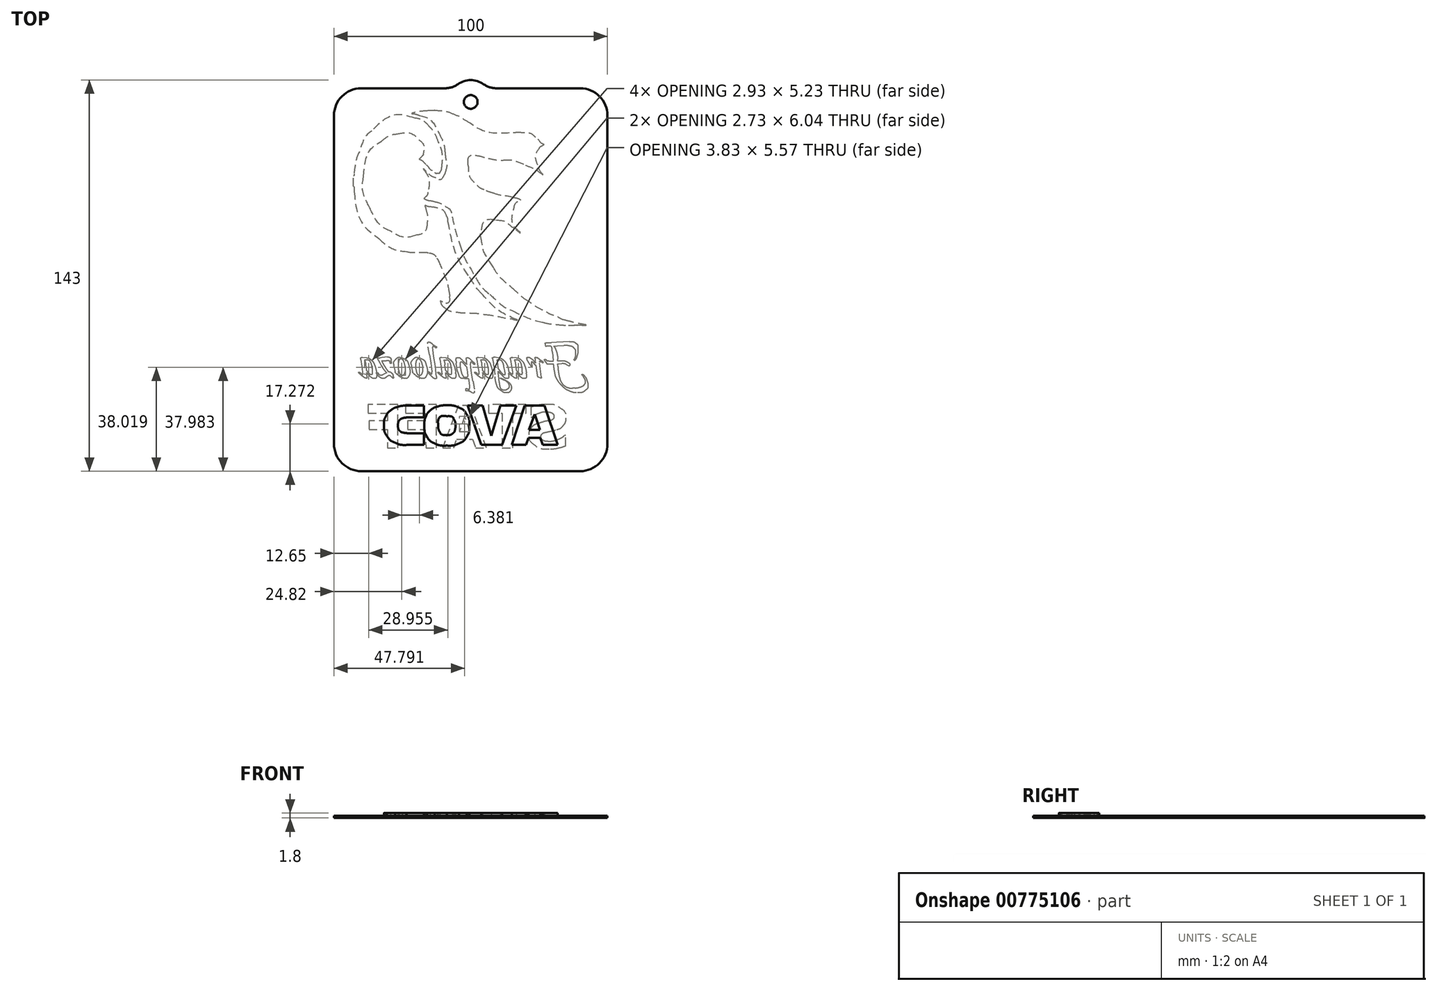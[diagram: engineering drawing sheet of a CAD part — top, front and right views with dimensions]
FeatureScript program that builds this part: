
annotation { "Feature Type Name" : "Feature", "Feature Type Description" : "" }
export const myFeature = defineFeature(function(context is Context, id is Id, definition is map)
    precondition{}
    {
        {
            var Q0;
            Q0=qCreatedBy(makeId("Top.planeOp"),FACE);
            var sketch = newSketch(context, id + "F0", { "sketchPlane" : qUnion([Q0])});
            skLineSegment(sketch, "E0.bottom", {"start": v(-40, 70) * mm, "end": v(-9.33, 70) * mm});
            skLineSegment(sketch, "E0.top", {"start": v(-40, -70) * mm, "end": v(40, -70) * mm});
            skLineSegment(sketch, "E0.left", {"start": v(-50, 60) * mm, "end": v(-50, -60) * mm});
            skLineSegment(sketch, "E0.right", {"start": v(50, 60) * mm, "end": v(50, -60) * mm});
            skPoint(sketch, "E0.middle", {"position": v(0, 0) * mm});
            skCircle(sketch, "E1", {"center": v(0, 65) * mm, "radius": 2.5 * mm});
            skPoint(sketch, "E2.visualSharp", {"position": v(-50, 70) * mm});
            skArc(sketch, "E2.filletArc", {"start": v(-40, 70) * mm, "mid": v(-47.07, 67.07) * mm, "end": v(-50, 60) * mm});
            skPoint(sketch, "E3.visualSharp", {"position": v(50, 70) * mm});
            skArc(sketch, "E3.filletArc", {"start": v(50, 60) * mm, "mid": v(47.07, 67.07) * mm, "end": v(40, 70) * mm});
            skPoint(sketch, "E4.visualSharp", {"position": v(50, -70) * mm});
            skArc(sketch, "E4.filletArc", {"start": v(40, -70) * mm, "mid": v(47.07, -67.07) * mm, "end": v(50, -60) * mm});
            skPoint(sketch, "E5.visualSharp", {"position": v(-50, -70) * mm});
            skArc(sketch, "E5.filletArc", {"start": v(-50, -60) * mm, "mid": v(-47.07, -67.07) * mm, "end": v(-40, -70) * mm});
            skArc(sketch, "E6", {"start": v(-4.66, 71.5) * mm, "mid": v(0, 73) * mm, "end": v(4.66, 71.5) * mm});
            skArc(sketch, "E7.filletArc", {"start": v(-9.33, 70) * mm, "mid": v(-6.88, 70.38) * mm, "end": v(-4.66, 71.5) * mm});
            skLineSegment(sketch, "E8", {"start": v(40, 70) * mm, "end": v(9.33, 70) * mm});
            skArc(sketch, "E9.filletArc", {"start": v(4.66, 71.5) * mm, "mid": v(6.88, 70.38) * mm, "end": v(9.33, 70) * mm});
            skSolve(sketch);
        }
        {
            var Q0;
            Q0=qCreatedBy(makeId("Top.planeOp"),FACE);
            var sketch = newSketch(context, id + "F1", { "sketchPlane" : qUnion([Q0])});
            skLineSegment(sketch, "E10", {"start": v(38.17, -16.7) * mm, "end": v(38.78, -16.7) * mm});
            skLineSegment(sketch, "E11", {"start": v(-13.07, 61.96) * mm, "end": v(-13.17, 61.96) * mm});
            skLineSegment(sketch, "E12", {"start": v(-14.17, 61.96) * mm, "end": v(-14.37, 61.96) * mm});
            skLineSegment(sketch, "E13", {"start": v(-42.85, 37.93) * mm, "end": v(-42.85, 36.81) * mm});
            skLineSegment(sketch, "E14", {"start": v(-42.85, 35.49) * mm, "end": v(-42.85, 34.98) * mm});
            skLineSegment(sketch, "E15", {"start": v(-42.85, 34.78) * mm, "end": v(-42.85, 34.16) * mm});
            skLineSegment(sketch, "E16", {"start": v(40.64, -16.7) * mm, "end": v(40.63, -16.62) * mm});
            skLineSegment(sketch, "E17", {"start": v(38.83, -16.7) * mm, "end": v(40.64, -16.7) * mm});
            skLineSegment(sketch, "E18", {"start": v(-42.85, 36.81) * mm, "end": v(-42.85, 35.49) * mm});
            skLineSegment(sketch, "E19", {"start": v(-13.21, 61.96) * mm, "end": v(-14.22, 61.96) * mm});
            skLineSegment(sketch, "E20", {"start": v(-42.85, 34.98) * mm, "end": v(-42.85, 34.77) * mm});
            skLineSegment(sketch, "E21", {"start": v(36.03, -31.52) * mm, "end": v(35.01, -30.98) * mm});
            skLineSegment(sketch, "E22", {"start": v(33.37, -30.7) * mm, "end": v(32.17, -30.75) * mm});
            skLineSegment(sketch, "E23", {"start": v(32.17, -30.75) * mm, "end": v(30.92, -30.82) * mm});
            skLineSegment(sketch, "E24", {"start": v(30.92, -30.82) * mm, "end": v(27.9, -30.82) * mm});
            skLineSegment(sketch, "E25", {"start": v(27.9, -30.82) * mm, "end": v(27.52, -30.26) * mm});
            skLineSegment(sketch, "E26", {"start": v(26.88, -29.35) * mm, "end": v(26.9, -29.28) * mm});
            skLineSegment(sketch, "E27", {"start": v(30.32, -29.76) * mm, "end": v(31.57, -29.76) * mm});
            skLineSegment(sketch, "E28", {"start": v(31.57, -29.76) * mm, "end": v(33.15, -29.76) * mm});
            skLineSegment(sketch, "E29", {"start": v(33.15, -29.76) * mm, "end": v(34.41, -29.76) * mm});
            skLineSegment(sketch, "E30", {"start": v(34.05, -24.06) * mm, "end": v(31.6, -24.16) * mm});
            skLineSegment(sketch, "E31", {"start": v(31.6, -24.16) * mm, "end": v(29.36, -24.3) * mm});
            skLineSegment(sketch, "E32", {"start": v(27.3, -24.39) * mm, "end": v(27.09, -23.13) * mm});
            skLineSegment(sketch, "E33", {"start": v(29.45, -22.97) * mm, "end": v(31.35, -22.93) * mm});
            skLineSegment(sketch, "E34", {"start": v(31.35, -22.93) * mm, "end": v(33.78, -22.78) * mm});
            skLineSegment(sketch, "E35", {"start": v(33.78, -22.78) * mm, "end": v(36.14, -22.66) * mm});
            skLineSegment(sketch, "E36", {"start": v(38.04, -29.5) * mm, "end": v(37.7, -29.32) * mm});
            skLineSegment(sketch, "E37", {"start": v(30.25, -30.2) * mm, "end": v(29.88, -26.54) * mm});
            skLineSegment(sketch, "E38", {"start": v(29.55, -24.56) * mm, "end": v(29.3, -24.3) * mm});
            skLineSegment(sketch, "E39", {"start": v(29.18, -23.96) * mm, "end": v(29.55, -24.04) * mm});
            skLineSegment(sketch, "E40", {"start": v(31.76, -29.06) * mm, "end": v(31.88, -31.82) * mm});
            skLineSegment(sketch, "E41", {"start": v(37.27, -39.71) * mm, "end": v(38.3, -39.63) * mm});
            skLineSegment(sketch, "E42", {"start": v(41.15, -35.4) * mm, "end": v(40.78, -34.92) * mm});
            skLineSegment(sketch, "E43", {"start": v(40.78, -34.92) * mm, "end": v(40.72, -34.76) * mm});
            skLineSegment(sketch, "E44", {"start": v(23.56, -29.53) * mm, "end": v(23.5, -28.89) * mm});
            skLineSegment(sketch, "E45", {"start": v(24.23, -28.54) * mm, "end": v(25.22, -29.23) * mm});
            skLineSegment(sketch, "E46", {"start": v(25.22, -29.23) * mm, "end": v(26.33, -30.01) * mm});
            skLineSegment(sketch, "E47", {"start": v(26.48, -30.3) * mm, "end": v(26.4, -30.34) * mm});
            skLineSegment(sketch, "E48", {"start": v(26.4, -30.34) * mm, "end": v(26.3, -30.32) * mm});
            skLineSegment(sketch, "E49", {"start": v(26.3, -30.32) * mm, "end": v(26.17, -30.3) * mm});
            skLineSegment(sketch, "E50", {"start": v(25.15, -30.3) * mm, "end": v(25.53, -33.54) * mm});
            skLineSegment(sketch, "E51", {"start": v(25.53, -33.54) * mm, "end": v(25.79, -35.64) * mm});
            skLineSegment(sketch, "E52", {"start": v(25.88, -36) * mm, "end": v(24.4, -35.44) * mm});
            skLineSegment(sketch, "E53", {"start": v(23.19, -29.85) * mm, "end": v(23.89, -30.75) * mm});
            skLineSegment(sketch, "E54", {"start": v(23.65, -31.18) * mm, "end": v(23.19, -30.77) * mm});
            skLineSegment(sketch, "E55", {"start": v(15.9, -29.4) * mm, "end": v(15.4, -29.4) * mm});
            skLineSegment(sketch, "E56", {"start": v(15.4, -29.4) * mm, "end": v(15.02, -29.33) * mm});
            skLineSegment(sketch, "E57", {"start": v(15.24, -28.42) * mm, "end": v(16.71, -28.55) * mm});
            skLineSegment(sketch, "E58", {"start": v(17.3, -34.56) * mm, "end": v(16.63, -33.84) * mm});
            skLineSegment(sketch, "E59", {"start": v(16.01, -32.3) * mm, "end": v(16.46, -32.84) * mm});
            skLineSegment(sketch, "E60", {"start": v(16.96, -29.4) * mm, "end": v(16.5, -29.4) * mm});
            skLineSegment(sketch, "E61", {"start": v(16.5, -29.4) * mm, "end": v(15.9, -29.4) * mm});
            skLineSegment(sketch, "E62", {"start": v(16.38, -31.1) * mm, "end": v(16.6, -32.79) * mm});
            skLineSegment(sketch, "E63", {"start": v(16.6, -32.79) * mm, "end": v(16.8, -34.4) * mm});
            skLineSegment(sketch, "E64", {"start": v(16.8, -34.4) * mm, "end": v(16.85, -35.3) * mm});
            skLineSegment(sketch, "E65", {"start": v(14.85, -34.45) * mm, "end": v(15.26, -34.75) * mm});
            skLineSegment(sketch, "E66", {"start": v(15.33, -34.51) * mm, "end": v(15.26, -33.72) * mm});
            skLineSegment(sketch, "E67", {"start": v(15.26, -33.72) * mm, "end": v(14.93, -31.64) * mm});
            skLineSegment(sketch, "E68", {"start": v(14.93, -31.64) * mm, "end": v(14.54, -29.14) * mm});
            skLineSegment(sketch, "E69", {"start": v(9.13, -29.4) * mm, "end": v(8.63, -29.4) * mm});
            skLineSegment(sketch, "E70", {"start": v(8.63, -29.4) * mm, "end": v(8.27, -29.31) * mm});
            skLineSegment(sketch, "E71", {"start": v(8.04, -29.08) * mm, "end": v(7.89, -28.74) * mm});
            skLineSegment(sketch, "E72", {"start": v(8.47, -28.35) * mm, "end": v(8.95, -28.35) * mm});
            skLineSegment(sketch, "E73", {"start": v(8.95, -28.35) * mm, "end": v(9.46, -28.52) * mm});
            skLineSegment(sketch, "E74", {"start": v(9.46, -28.52) * mm, "end": v(10.14, -28.6) * mm});
            skLineSegment(sketch, "E75", {"start": v(11.28, -34.74) * mm, "end": v(10.47, -33.88) * mm});
            skLineSegment(sketch, "E76", {"start": v(9.69, -32.05) * mm, "end": v(10.37, -32.95) * mm});
            skLineSegment(sketch, "E77", {"start": v(10.37, -32.95) * mm, "end": v(11.14, -33.94) * mm});
            skLineSegment(sketch, "E78", {"start": v(12.6, -34.13) * mm, "end": v(12.52, -33.32) * mm});
            skLineSegment(sketch, "E79", {"start": v(12.52, -33.32) * mm, "end": v(12.29, -32.26) * mm});
            skLineSegment(sketch, "E80", {"start": v(12.29, -32.26) * mm, "end": v(12.13, -31.6) * mm});
            skLineSegment(sketch, "E81", {"start": v(10.33, -29.4) * mm, "end": v(9.77, -29.4) * mm});
            skLineSegment(sketch, "E82", {"start": v(9.77, -29.4) * mm, "end": v(9.13, -29.4) * mm});
            skLineSegment(sketch, "E83", {"start": v(9.46, -28.84) * mm, "end": v(9.77, -30.97) * mm});
            skLineSegment(sketch, "E84", {"start": v(9.77, -30.97) * mm, "end": v(10.1, -34.04) * mm});
            skLineSegment(sketch, "E85", {"start": v(10.1, -34.04) * mm, "end": v(10.34, -36.29) * mm});
            skLineSegment(sketch, "E86", {"start": v(10.34, -36.29) * mm, "end": v(10.47, -37.68) * mm});
            skLineSegment(sketch, "E87", {"start": v(12.25, -36.7) * mm, "end": v(11.22, -36.28) * mm});
            skLineSegment(sketch, "E88", {"start": v(10.66, -36) * mm, "end": v(10.7, -35.94) * mm});
            skLineSegment(sketch, "E89", {"start": v(8.88, -35.3) * mm, "end": v(8.5, -31.75) * mm});
            skLineSegment(sketch, "E90", {"start": v(3.54, -29.4) * mm, "end": v(3.04, -29.4) * mm});
            skLineSegment(sketch, "E91", {"start": v(3.04, -29.4) * mm, "end": v(2.67, -29.33) * mm});
            skLineSegment(sketch, "E92", {"start": v(2.88, -28.42) * mm, "end": v(4.36, -28.55) * mm});
            skLineSegment(sketch, "E93", {"start": v(4.94, -34.56) * mm, "end": v(4.28, -33.84) * mm});
            skLineSegment(sketch, "E94", {"start": v(3.66, -32.3) * mm, "end": v(4.1, -32.84) * mm});
            skLineSegment(sketch, "E95", {"start": v(4.6, -29.4) * mm, "end": v(4.14, -29.4) * mm});
            skLineSegment(sketch, "E96", {"start": v(4.14, -29.4) * mm, "end": v(3.54, -29.4) * mm});
            skLineSegment(sketch, "E97", {"start": v(4.02, -31.1) * mm, "end": v(4.25, -32.79) * mm});
            skLineSegment(sketch, "E98", {"start": v(4.25, -32.79) * mm, "end": v(4.44, -34.4) * mm});
            skLineSegment(sketch, "E99", {"start": v(4.44, -34.4) * mm, "end": v(4.5, -35.3) * mm});
            skLineSegment(sketch, "E100", {"start": v(2.5, -34.45) * mm, "end": v(2.9, -34.75) * mm});
            skLineSegment(sketch, "E101", {"start": v(2.98, -34.51) * mm, "end": v(2.9, -33.72) * mm});
            skLineSegment(sketch, "E102", {"start": v(2.9, -33.72) * mm, "end": v(2.58, -31.64) * mm});
            skLineSegment(sketch, "E103", {"start": v(2.58, -31.64) * mm, "end": v(2.19, -29.14) * mm});
            skLineSegment(sketch, "E104", {"start": v(-0.07, -30.77) * mm, "end": v(0.03, -32.01) * mm});
            skLineSegment(sketch, "E105", {"start": v(0.03, -32.01) * mm, "end": v(0.35, -34.14) * mm});
            skLineSegment(sketch, "E106", {"start": v(0.35, -34.14) * mm, "end": v(0.85, -37.11) * mm});
            skLineSegment(sketch, "E107", {"start": v(0.96, -41.4) * mm, "end": v(0.32, -41.16) * mm});
            skLineSegment(sketch, "E108", {"start": v(-0.43, -39.67) * mm, "end": v(-0.47, -38.83) * mm});
            skLineSegment(sketch, "E109", {"start": v(-0.47, -38.83) * mm, "end": v(-0.77, -36.7) * mm});
            skLineSegment(sketch, "E110", {"start": v(-0.77, -36.7) * mm, "end": v(-1.14, -33.74) * mm});
            skLineSegment(sketch, "E111", {"start": v(-1.14, -33.74) * mm, "end": v(-1.34, -32.16) * mm});
            skLineSegment(sketch, "E112", {"start": v(-1.34, -32.16) * mm, "end": v(-1.56, -30.34) * mm});
            skLineSegment(sketch, "E113", {"start": v(-1.56, -30.34) * mm, "end": v(-1.62, -29.37) * mm});
            skLineSegment(sketch, "E114", {"start": v(-0.41, -35.45) * mm, "end": v(-0.36, -35.65) * mm});
            skLineSegment(sketch, "E115", {"start": v(-0.18, -36.1) * mm, "end": v(-0.24, -36.16) * mm});
            skLineSegment(sketch, "E116", {"start": v(-0.24, -36.16) * mm, "end": v(-0.31, -36.19) * mm});
            skLineSegment(sketch, "E117", {"start": v(-0.31, -36.19) * mm, "end": v(-0.7, -36.11) * mm});
            skLineSegment(sketch, "E118", {"start": v(-0.7, -36.11) * mm, "end": v(-1.4, -36.11) * mm});
            skLineSegment(sketch, "E119", {"start": v(-1.4, -36.11) * mm, "end": v(-2.27, -36.11) * mm});
            skLineSegment(sketch, "E120", {"start": v(-2.53, -30.03) * mm, "end": v(-1.85, -30.67) * mm});
            skLineSegment(sketch, "E121", {"start": v(-9.94, -29.4) * mm, "end": v(-10.44, -29.4) * mm});
            skLineSegment(sketch, "E122", {"start": v(-10.44, -29.4) * mm, "end": v(-10.8, -29.33) * mm});
            skLineSegment(sketch, "E123", {"start": v(-10.6, -28.42) * mm, "end": v(-9.12, -28.55) * mm});
            skLineSegment(sketch, "E124", {"start": v(-8.54, -34.56) * mm, "end": v(-9.2, -33.84) * mm});
            skLineSegment(sketch, "E125", {"start": v(-9.82, -32.3) * mm, "end": v(-9.37, -32.84) * mm});
            skLineSegment(sketch, "E126", {"start": v(-8.87, -29.4) * mm, "end": v(-9.34, -29.4) * mm});
            skLineSegment(sketch, "E127", {"start": v(-9.34, -29.4) * mm, "end": v(-9.94, -29.4) * mm});
            skLineSegment(sketch, "E128", {"start": v(-9.46, -31.1) * mm, "end": v(-9.23, -32.79) * mm});
            skLineSegment(sketch, "E129", {"start": v(-9.23, -32.79) * mm, "end": v(-9.04, -34.4) * mm});
            skLineSegment(sketch, "E130", {"start": v(-9.04, -34.4) * mm, "end": v(-8.99, -35.3) * mm});
            skLineSegment(sketch, "E131", {"start": v(-10.98, -34.45) * mm, "end": v(-10.58, -34.75) * mm});
            skLineSegment(sketch, "E132", {"start": v(-10.5, -34.51) * mm, "end": v(-10.58, -33.72) * mm});
            skLineSegment(sketch, "E133", {"start": v(-10.58, -33.72) * mm, "end": v(-10.9, -31.64) * mm});
            skLineSegment(sketch, "E134", {"start": v(-10.9, -31.64) * mm, "end": v(-11.29, -29.14) * mm});
            skLineSegment(sketch, "E135", {"start": v(-14.16, -33.74) * mm, "end": v(-14.26, -32.52) * mm});
            skLineSegment(sketch, "E136", {"start": v(-14.26, -32.52) * mm, "end": v(-14.56, -30.46) * mm});
            skLineSegment(sketch, "E137", {"start": v(-14.56, -30.46) * mm, "end": v(-15.08, -27.43) * mm});
            skLineSegment(sketch, "E138", {"start": v(-15, -22.92) * mm, "end": v(-14.03, -23.56) * mm});
            skLineSegment(sketch, "E139", {"start": v(-12.63, -24.87) * mm, "end": v(-12.86, -24.8) * mm});
            skLineSegment(sketch, "E140", {"start": v(-13.91, -24.76) * mm, "end": v(-13.85, -25.5) * mm});
            skLineSegment(sketch, "E141", {"start": v(-13.85, -25.5) * mm, "end": v(-13.65, -26.9) * mm});
            skLineSegment(sketch, "E142", {"start": v(-13.65, -26.9) * mm, "end": v(-13.36, -28.73) * mm});
            skLineSegment(sketch, "E143", {"start": v(-13.36, -28.73) * mm, "end": v(-13.08, -30.79) * mm});
            skLineSegment(sketch, "E144", {"start": v(-13.08, -30.79) * mm, "end": v(-12.8, -32.84) * mm});
            skLineSegment(sketch, "E145", {"start": v(-12.8, -32.84) * mm, "end": v(-12.61, -34.45) * mm});
            skLineSegment(sketch, "E146", {"start": v(-12.61, -34.45) * mm, "end": v(-12.55, -35.39) * mm});
            skLineSegment(sketch, "E147", {"start": v(-19.13, -35.54) * mm, "end": v(-20.12, -34.9) * mm});
            skLineSegment(sketch, "E148", {"start": v(-21.26, -33.55) * mm, "end": v(-21.5, -32.5) * mm});
            skLineSegment(sketch, "E149", {"start": v(-21.5, -32.5) * mm, "end": v(-21.73, -31.52) * mm});
            skLineSegment(sketch, "E150", {"start": v(-21.73, -31.52) * mm, "end": v(-21.79, -30.84) * mm});
            skLineSegment(sketch, "E151", {"start": v(-19.8, -28.37) * mm, "end": v(-19.36, -28.42) * mm});
            skLineSegment(sketch, "E152", {"start": v(-19.36, -28.42) * mm, "end": v(-18.37, -28.75) * mm});
            skLineSegment(sketch, "E153", {"start": v(-17.54, -31.66) * mm, "end": v(-18, -30.05) * mm});
            skLineSegment(sketch, "E154", {"start": v(-25.5, -35.54) * mm, "end": v(-26.5, -34.9) * mm});
            skLineSegment(sketch, "E155", {"start": v(-27.64, -33.55) * mm, "end": v(-27.88, -32.5) * mm});
            skLineSegment(sketch, "E156", {"start": v(-27.88, -32.5) * mm, "end": v(-28.1, -31.52) * mm});
            skLineSegment(sketch, "E157", {"start": v(-28.1, -31.52) * mm, "end": v(-28.17, -30.84) * mm});
            skLineSegment(sketch, "E158", {"start": v(-26.19, -28.37) * mm, "end": v(-25.74, -28.42) * mm});
            skLineSegment(sketch, "E159", {"start": v(-25.74, -28.42) * mm, "end": v(-24.75, -28.75) * mm});
            skLineSegment(sketch, "E160", {"start": v(-23.92, -31.66) * mm, "end": v(-24.38, -30.05) * mm});
            skLineSegment(sketch, "E161", {"start": v(-30.82, -29.63) * mm, "end": v(-31.6, -29.66) * mm});
            skLineSegment(sketch, "E162", {"start": v(-31.6, -29.66) * mm, "end": v(-32.28, -29.63) * mm});
            skLineSegment(sketch, "E163", {"start": v(-32.28, -29.63) * mm, "end": v(-32.6, -29.59) * mm});
            skLineSegment(sketch, "E164", {"start": v(-28.05, -35.7) * mm, "end": v(-28.34, -36) * mm});
            skLineSegment(sketch, "E165", {"start": v(-32.16, -32.19) * mm, "end": v(-32.67, -31.4) * mm});
            skLineSegment(sketch, "E166", {"start": v(-32.67, -31.4) * mm, "end": v(-33.23, -30.44) * mm});
            skLineSegment(sketch, "E167", {"start": v(-33.23, -30.44) * mm, "end": v(-33.8, -29.45) * mm});
            skLineSegment(sketch, "E168", {"start": v(-33.8, -29.45) * mm, "end": v(-34.28, -28.64) * mm});
            skLineSegment(sketch, "E169", {"start": v(-34.18, -28.33) * mm, "end": v(-34.02, -28.38) * mm});
            skLineSegment(sketch, "E170", {"start": v(-33.17, -28.56) * mm, "end": v(-32.43, -28.52) * mm});
            skLineSegment(sketch, "E171", {"start": v(-32.43, -28.52) * mm, "end": v(-31.52, -28.4) * mm});
            skLineSegment(sketch, "E172", {"start": v(-31.52, -28.4) * mm, "end": v(-30.4, -28.23) * mm});
            skLineSegment(sketch, "E173", {"start": v(-29.1, -29.33) * mm, "end": v(-29.02, -30) * mm});
            skLineSegment(sketch, "E174", {"start": v(-28.09, -35.68) * mm, "end": v(-28.22, -35.85) * mm});
            skLineSegment(sketch, "E175", {"start": v(-28.4, -35.95) * mm, "end": v(-29.27, -35.27) * mm});
            skLineSegment(sketch, "E176", {"start": v(-32.12, -34.67) * mm, "end": v(-31.13, -34.22) * mm});
            skLineSegment(sketch, "E177", {"start": v(-31.13, -34.22) * mm, "end": v(-30.22, -33.8) * mm});
            skLineSegment(sketch, "E178", {"start": v(-28.36, -35.08) * mm, "end": v(-28.32, -35.29) * mm});
            skLineSegment(sketch, "E179", {"start": v(-28.32, -35.29) * mm, "end": v(-28.26, -35.48) * mm});
            skLineSegment(sketch, "E180", {"start": v(-28.26, -35.48) * mm, "end": v(-28.09, -35.68) * mm});
            skLineSegment(sketch, "E181", {"start": v(-38.9, -29.4) * mm, "end": v(-39.4, -29.4) * mm});
            skLineSegment(sketch, "E182", {"start": v(-39.4, -29.4) * mm, "end": v(-39.76, -29.33) * mm});
            skLineSegment(sketch, "E183", {"start": v(-39.55, -28.42) * mm, "end": v(-38.08, -28.55) * mm});
            skLineSegment(sketch, "E184", {"start": v(-37.5, -34.56) * mm, "end": v(-38.15, -33.84) * mm});
            skLineSegment(sketch, "E185", {"start": v(-38.77, -32.3) * mm, "end": v(-38.33, -32.84) * mm});
            skLineSegment(sketch, "E186", {"start": v(-37.82, -29.4) * mm, "end": v(-38.3, -29.4) * mm});
            skLineSegment(sketch, "E187", {"start": v(-38.3, -29.4) * mm, "end": v(-38.9, -29.4) * mm});
            skLineSegment(sketch, "E188", {"start": v(-38.41, -31.1) * mm, "end": v(-38.19, -32.79) * mm});
            skLineSegment(sketch, "E189", {"start": v(-38.19, -32.79) * mm, "end": v(-38, -34.4) * mm});
            skLineSegment(sketch, "E190", {"start": v(-38, -34.4) * mm, "end": v(-37.94, -35.3) * mm});
            skLineSegment(sketch, "E191", {"start": v(-39.94, -34.45) * mm, "end": v(-39.53, -34.75) * mm});
            skLineSegment(sketch, "E192", {"start": v(-39.45, -34.51) * mm, "end": v(-39.53, -33.72) * mm});
            skLineSegment(sketch, "E193", {"start": v(-39.53, -33.72) * mm, "end": v(-39.86, -31.64) * mm});
            skLineSegment(sketch, "E194", {"start": v(-39.86, -31.64) * mm, "end": v(-40.24, -29.14) * mm});
            skLineSegment(sketch, "E195", {"start": v(22.49, -50.22) * mm, "end": v(22.06, -50.22) * mm});
            skLineSegment(sketch, "E196", {"start": v(22.06, -50.22) * mm, "end": v(22.06, -46.56) * mm});
            skLineSegment(sketch, "E197", {"start": v(34.32, -56.92) * mm, "end": v(34.76, -56.92) * mm});
            skLineSegment(sketch, "E198", {"start": v(34.76, -56.92) * mm, "end": v(34.76, -60.73) * mm});
            skLineSegment(sketch, "E199", {"start": v(6.54, -45.64) * mm, "end": v(20.3, -45.64) * mm});
            skLineSegment(sketch, "E200", {"start": v(20.3, -45.64) * mm, "end": v(20.3, -48.81) * mm});
            skLineSegment(sketch, "E201", {"start": v(20.3, -48.81) * mm, "end": v(15.36, -48.81) * mm});
            skLineSegment(sketch, "E202", {"start": v(15.36, -48.81) * mm, "end": v(15.36, -61.51) * mm});
            skLineSegment(sketch, "E203", {"start": v(15.36, -61.51) * mm, "end": v(11.47, -61.51) * mm});
            skLineSegment(sketch, "E204", {"start": v(11.47, -61.51) * mm, "end": v(11.47, -48.81) * mm});
            skLineSegment(sketch, "E205", {"start": v(11.47, -48.81) * mm, "end": v(6.54, -48.81) * mm});
            skLineSegment(sketch, "E206", {"start": v(6.54, -48.81) * mm, "end": v(6.54, -45.64) * mm});
            skLineSegment(sketch, "E207", {"start": v(-4.56, -45.99) * mm, "end": v(0.04, -45.99) * mm});
            skLineSegment(sketch, "E208", {"start": v(0.04, -45.99) * mm, "end": v(5.78, -61.51) * mm});
            skLineSegment(sketch, "E209", {"start": v(5.78, -61.51) * mm, "end": v(1.8, -61.51) * mm});
            skLineSegment(sketch, "E210", {"start": v(1.8, -61.51) * mm, "end": v(0.7, -58.34) * mm});
            skLineSegment(sketch, "E211", {"start": v(0.7, -58.34) * mm, "end": v(-5.12, -58.34) * mm});
            skLineSegment(sketch, "E212", {"start": v(-5.12, -58.34) * mm, "end": v(-6.2, -61.51) * mm});
            skLineSegment(sketch, "E213", {"start": v(-6.2, -61.51) * mm, "end": v(-10.3, -61.51) * mm});
            skLineSegment(sketch, "E214", {"start": v(-10.3, -61.51) * mm, "end": v(-4.56, -45.99) * mm});
            skLineSegment(sketch, "E215", {"start": v(-0.3, -55.51) * mm, "end": v(-2.2, -49.94) * mm});
            skLineSegment(sketch, "E216", {"start": v(-2.2, -49.94) * mm, "end": v(-4.12, -55.51) * mm});
            skLineSegment(sketch, "E217", {"start": v(-4.12, -55.51) * mm, "end": v(-0.3, -55.51) * mm});
            skLineSegment(sketch, "E218", {"start": v(-23.8, -45.64) * mm, "end": v(-12.51, -45.64) * mm});
            skLineSegment(sketch, "E219", {"start": v(-12.51, -45.64) * mm, "end": v(-12.51, -61.51) * mm});
            skLineSegment(sketch, "E220", {"start": v(-12.51, -61.51) * mm, "end": v(-16.4, -61.51) * mm});
            skLineSegment(sketch, "E221", {"start": v(-16.4, -61.51) * mm, "end": v(-16.75, -54.8) * mm});
            skLineSegment(sketch, "E222", {"start": v(-16.75, -54.8) * mm, "end": v(-23.1, -54.8) * mm});
            skLineSegment(sketch, "E223", {"start": v(-23.1, -54.8) * mm, "end": v(-23.1, -51.63) * mm});
            skLineSegment(sketch, "E224", {"start": v(-23.1, -51.63) * mm, "end": v(-16.75, -51.63) * mm});
            skLineSegment(sketch, "E225", {"start": v(-16.75, -51.63) * mm, "end": v(-16.75, -48.81) * mm});
            skLineSegment(sketch, "E226", {"start": v(-16.75, -48.81) * mm, "end": v(-23.8, -48.81) * mm});
            skLineSegment(sketch, "E227", {"start": v(-23.8, -48.81) * mm, "end": v(-23.8, -45.64) * mm});
            skLineSegment(sketch, "E228", {"start": v(-37.56, -45.64) * mm, "end": v(-26.63, -45.64) * mm});
            skLineSegment(sketch, "E229", {"start": v(-26.63, -45.64) * mm, "end": v(-26.63, -61.51) * mm});
            skLineSegment(sketch, "E230", {"start": v(-26.63, -61.51) * mm, "end": v(-30.5, -61.51) * mm});
            skLineSegment(sketch, "E231", {"start": v(-30.5, -61.51) * mm, "end": v(-30.5, -54.8) * mm});
            skLineSegment(sketch, "E232", {"start": v(-30.5, -54.8) * mm, "end": v(-37.2, -54.8) * mm});
            skLineSegment(sketch, "E233", {"start": v(-37.2, -54.8) * mm, "end": v(-37.2, -51.63) * mm});
            skLineSegment(sketch, "E234", {"start": v(-37.2, -51.63) * mm, "end": v(-30.5, -51.63) * mm});
            skLineSegment(sketch, "E235", {"start": v(-30.5, -51.63) * mm, "end": v(-30.5, -48.81) * mm});
            skLineSegment(sketch, "E236", {"start": v(-30.5, -48.81) * mm, "end": v(-37.56, -48.81) * mm});
            skLineSegment(sketch, "E237", {"start": v(-37.56, -48.81) * mm, "end": v(-37.56, -45.64) * mm});
            skFitSpline(sketch, "E238", {"points": [v(-14.37, 61.96) * mm, v(-14.8, 61.78) * mm, v(-15.26, 61.8) * mm, v(-15.71, 61.76) * mm]});
            skFitSpline(sketch, "E239", {"points": [v(-15.71, 61.76) * mm, v(-17.53, 61.62) * mm, v(-19.32, 61.38) * mm, v(-21.1, 60.93) * mm]});
            skFitSpline(sketch, "E240", {"points": [v(-21.1, 60.93) * mm, v(-21.24, 60.9) * mm, v(-21.43, 60.9) * mm, v(-21.54, 60.66) * mm]});
            skFitSpline(sketch, "E241", {"points": [v(-21.54, 60.66) * mm, v(-20.54, 60.63) * mm, v(-19.62, 60.35) * mm, v(-18.7, 60.03) * mm]});
            skFitSpline(sketch, "E242", {"points": [v(-18.7, 60.03) * mm, v(-15.38, 58.87) * mm, v(-13.15, 56.52) * mm, v(-11.58, 53.44) * mm]});
            skFitSpline(sketch, "E243", {"points": [v(-11.58, 53.44) * mm, v(-10.47, 51.29) * mm, v(-9.71, 49) * mm, v(-9.41, 46.6) * mm]});
            skFitSpline(sketch, "E244", {"points": [v(-9.41, 46.6) * mm, v(-9.11, 44.15) * mm, v(-8.77, 41.68) * mm, v(-9.35, 39.2) * mm]});
            skFitSpline(sketch, "E245", {"points": [v(-9.35, 39.2) * mm, v(-9.4, 38.94) * mm, v(-9.5, 38.7) * mm, v(-9.63, 38.47) * mm]});
            skFitSpline(sketch, "E246", {"points": [v(-9.63, 38.47) * mm, v(-10.22, 37.39) * mm, v(-11.1, 36.57) * mm, v(-12.72, 37.2) * mm]});
            skFitSpline(sketch, "E247", {"points": [v(-12.72, 37.2) * mm, v(-14.12, 37.75) * mm, v(-15.28, 38.64) * mm, v(-16.36, 39.65) * mm]});
            skFitSpline(sketch, "E248", {"points": [v(-16.36, 39.65) * mm, v(-16.66, 39.92) * mm, v(-16.91, 40.23) * mm, v(-17.25, 40.59) * mm]});
            skFitSpline(sketch, "E249", {"points": [v(-17.25, 40.59) * mm, v(-17.26, 40.3) * mm, v(-17.11, 40.19) * mm, v(-17.03, 40.05) * mm]});
            skFitSpline(sketch, "E250", {"points": [v(-17.03, 40.05) * mm, v(-15.47, 37.53) * mm, v(-15.17, 34.78) * mm, v(-15.68, 31.91) * mm]});
            skFitSpline(sketch, "E251", {"points": [v(-15.68, 31.91) * mm, v(-15.8, 31.24) * mm, v(-16.1, 30.64) * mm, v(-16.6, 30.16) * mm]});
            skFitSpline(sketch, "E252", {"points": [v(-16.6, 30.16) * mm, v(-17.12, 29.67) * mm, v(-17.1, 29.65) * mm, v(-16.44, 29.37) * mm]});
            skFitSpline(sketch, "E253", {"points": [v(-16.44, 29.37) * mm, v(-15.51, 28.97) * mm, v(-14.51, 28.87) * mm, v(-13.54, 28.62) * mm]});
            skFitSpline(sketch, "E254", {"points": [v(-13.54, 28.62) * mm, v(-11.87, 28.2) * mm, v(-10.3, 27.56) * mm, v(-8.86, 26.56) * mm]});
            skFitSpline(sketch, "E255", {"points": [v(-8.86, 26.56) * mm, v(-7.66, 25.72) * mm, v(-7.05, 24.5) * mm, v(-6.77, 23.12) * mm]});
            skFitSpline(sketch, "E256", {"points": [v(-6.77, 23.12) * mm, v(-6.07, 19.68) * mm, v(-5.15, 16.3) * mm, v(-4.03, 13) * mm]});
            skFitSpline(sketch, "E257", {"points": [v(-4.03, 13) * mm, v(-3.06, 10.12) * mm, v(-1.94, 7.3) * mm, v(-0.43, 4.69) * mm]});
            skFitSpline(sketch, "E258", {"points": [v(-0.43, 4.69) * mm, v(1.68, 1.04) * mm, v(3.89, -2.54) * mm, v(7.02, -5.42) * mm]});
            skFitSpline(sketch, "E259", {"points": [v(7.02, -5.42) * mm, v(9.48, -7.68) * mm, v(12.02, -9.8) * mm, v(15.04, -11.25) * mm]});
            skFitSpline(sketch, "E260", {"points": [v(15.04, -11.25) * mm, v(18.76, -13.03) * mm, v(22.58, -14.59) * mm, v(26.59, -15.61) * mm]});
            skFitSpline(sketch, "E261", {"points": [v(26.59, -15.61) * mm, v(28.25, -16.04) * mm, v(29.96, -16.23) * mm, v(31.67, -16.4) * mm]});
            skFitSpline(sketch, "E262", {"points": [v(31.67, -16.4) * mm, v(33.03, -16.54) * mm, v(34.4, -16.62) * mm, v(35.77, -16.62) * mm]});
            skFitSpline(sketch, "E263", {"points": [v(35.77, -16.62) * mm, v(36.22, -16.7) * mm, v(36.67, -16.64) * mm, v(37.13, -16.66) * mm]});
            skFitSpline(sketch, "E264", {"points": [v(37.13, -16.66) * mm, v(37.48, -16.68) * mm, v(37.83, -16.6) * mm, v(38.17, -16.7) * mm]});
            skFitSpline(sketch, "E265", {"points": [v(38.78, -16.7) * mm, v(39.38, -16.6) * mm, v(39.99, -16.69) * mm, v(40.59, -16.66) * mm]});
            skFitSpline(sketch, "E266", {"points": [v(40.59, -16.66) * mm, v(41.03, -16.65) * mm, v(41.48, -16.66) * mm, v(41.92, -16.65) * mm]});
            skFitSpline(sketch, "E267", {"points": [v(41.92, -16.65) * mm, v(42.02, -16.65) * mm, v(42.17, -16.71) * mm, v(42.18, -16.52) * mm]});
            skFitSpline(sketch, "E268", {"points": [v(42.18, -16.52) * mm, v(40.35, -16.18) * mm, v(38.52, -15.83) * mm, v(36.71, -15.35) * mm]});
            skFitSpline(sketch, "E269", {"points": [v(36.71, -15.35) * mm, v(36, -15.16) * mm, v(35.25, -15.03) * mm, v(34.53, -14.82) * mm]});
            skFitSpline(sketch, "E270", {"points": [v(34.53, -14.82) * mm, v(33.1, -14.38) * mm, v(31.81, -13.6) * mm, v(30.4, -13.1) * mm]});
            skFitSpline(sketch, "E271", {"points": [v(30.4, -13.1) * mm, v(28.9, -12.57) * mm, v(27.54, -11.75) * mm, v(26.13, -11.04) * mm]});
            skFitSpline(sketch, "E272", {"points": [v(26.13, -11.04) * mm, v(24.28, -10.1) * mm, v(22.61, -8.9) * mm, v(20.9, -7.78) * mm]});
            skFitSpline(sketch, "E273", {"points": [v(20.9, -7.78) * mm, v(19.32, -6.73) * mm, v(17.87, -5.46) * mm, v(16.43, -4.2) * mm]});
            skFitSpline(sketch, "E274", {"points": [v(16.43, -4.2) * mm, v(13.43, -1.57) * mm, v(10.5, 1.14) * mm, v(8.29, 4.51) * mm]});
            skFitSpline(sketch, "E275", {"points": [v(8.29, 4.51) * mm, v(6.39, 7.4) * mm, v(4.75, 10.42) * mm, v(4.04, 13.87) * mm]});
            skFitSpline(sketch, "E276", {"points": [v(4.04, 13.87) * mm, v(3.74, 15.29) * mm, v(3.6, 16.77) * mm, v(3.96, 18.15) * mm]});
            skFitSpline(sketch, "E277", {"points": [v(3.96, 18.15) * mm, v(4.68, 20.94) * mm, v(6.59, 22.1) * mm, v(9.37, 21.76) * mm]});
            skFitSpline(sketch, "E278", {"points": [v(9.37, 21.76) * mm, v(12.14, 21.42) * mm, v(14.36, 19.9) * mm, v(16.53, 18.28) * mm]});
            skFitSpline(sketch, "E279", {"points": [v(16.53, 18.28) * mm, v(17.05, 17.9) * mm, v(17.55, 17.5) * mm, v(18.06, 17.1) * mm]});
            skFitSpline(sketch, "E280", {"points": [v(18.06, 17.1) * mm, v(18.14, 17.24) * mm, v(18.06, 17.27) * mm, v(18.02, 17.3) * mm]});
            skFitSpline(sketch, "E281", {"points": [v(18.02, 17.3) * mm, v(15.67, 19.8) * mm, v(15.1, 22.76) * mm, v(15.81, 26.03) * mm]});
            skFitSpline(sketch, "E282", {"points": [v(15.81, 26.03) * mm, v(16.12, 27.45) * mm, v(16.96, 28.48) * mm, v(18.36, 29.08) * mm]});
            skFitSpline(sketch, "E283", {"points": [v(18.36, 29.08) * mm, v(17.45, 29.57) * mm, v(16.52, 29.83) * mm, v(15.58, 30.04) * mm]});
            skFitSpline(sketch, "E284", {"points": [v(15.58, 30.04) * mm, v(13.22, 30.57) * mm, v(10.83, 30.9) * mm, v(8.5, 31.57) * mm]});
            skFitSpline(sketch, "E285", {"points": [v(8.5, 31.57) * mm, v(7.27, 31.92) * mm, v(6.07, 32.36) * mm, v(4.9, 32.88) * mm]});
            skFitSpline(sketch, "E286", {"points": [v(4.9, 32.88) * mm, v(3.5, 33.5) * mm, v(2.36, 34.42) * mm, v(1.34, 35.53) * mm]});
            skFitSpline(sketch, "E287", {"points": [v(1.34, 35.53) * mm, v(0.04, 36.96) * mm, v(-0.59, 38.66) * mm, v(-0.74, 40.57) * mm]});
            skFitSpline(sketch, "E288", {"points": [v(-0.74, 40.57) * mm, v(-0.8, 41.38) * mm, v(-1, 42.17) * mm, v(-0.94, 43) * mm]});
            skFitSpline(sketch, "E289", {"points": [v(-0.94, 43) * mm, v(-0.85, 44.55) * mm, v(0.53, 45.67) * mm, v(2.04, 45.42) * mm]});
            skFitSpline(sketch, "E290", {"points": [v(2.04, 45.42) * mm, v(3.57, 45.16) * mm, v(5.04, 44.69) * mm, v(6.55, 44.35) * mm]});
            skFitSpline(sketch, "E291", {"points": [v(6.55, 44.35) * mm, v(8.37, 43.95) * mm, v(10.2, 43.7) * mm, v(12.06, 43.72) * mm]});
            skFitSpline(sketch, "E292", {"points": [v(12.06, 43.72) * mm, v(14.87, 43.77) * mm, v(17.47, 42.99) * mm, v(20.03, 41.9) * mm]});
            skFitSpline(sketch, "E293", {"points": [v(20.03, 41.9) * mm, v(22.15, 41) * mm, v(24.19, 39.94) * mm, v(26.08, 38.6) * mm]});
            skFitSpline(sketch, "E294", {"points": [v(26.08, 38.6) * mm, v(26.17, 38.53) * mm, v(26.25, 38.43) * mm, v(26.44, 38.49) * mm]});
            skFitSpline(sketch, "E295", {"points": [v(26.44, 38.49) * mm, v(25.56, 39.48) * mm, v(24.9, 40.61) * mm, v(24.5, 41.84) * mm]});
            skFitSpline(sketch, "E296", {"points": [v(24.5, 41.84) * mm, v(23.83, 43.93) * mm, v(23.78, 46.02) * mm, v(25.03, 47.97) * mm]});
            skFitSpline(sketch, "E297", {"points": [v(25.03, 47.97) * mm, v(25.46, 48.64) * mm, v(26.12, 49) * mm, v(26.82, 49.4) * mm]});
            skFitSpline(sketch, "E298", {"points": [v(26.82, 49.4) * mm, v(25.63, 50.1) * mm, v(24.78, 51.15) * mm, v(23.76, 52) * mm]});
            skFitSpline(sketch, "E299", {"points": [v(23.76, 52) * mm, v(22.25, 53.27) * mm, v(20.44, 53.7) * mm, v(18.55, 53.75) * mm]});
            skFitSpline(sketch, "E300", {"points": [v(18.55, 53.75) * mm, v(17.1, 53.78) * mm, v(15.64, 53.72) * mm, v(14.19, 53.67) * mm]});
            skFitSpline(sketch, "E301", {"points": [v(14.19, 53.67) * mm, v(9.06, 53.52) * mm, v(4.2, 54.58) * mm, v(-0.26, 57.24) * mm]});
            skFitSpline(sketch, "E302", {"points": [v(-0.26, 57.24) * mm, v(-2.15, 58.37) * mm, v(-4.03, 59.52) * mm, v(-6.07, 60.37) * mm]});
            skFitSpline(sketch, "E303", {"points": [v(-6.07, 60.37) * mm, v(-8.01, 61.18) * mm, v(-10.04, 61.62) * mm, v(-12.13, 61.77) * mm]});
            skFitSpline(sketch, "E304", {"points": [v(-12.13, 61.77) * mm, v(-12.45, 61.8) * mm, v(-12.78, 61.8) * mm, v(-13.07, 61.96) * mm]});
            skFitSpline(sketch, "E305", {"points": [v(-13.17, 61.96) * mm, v(-13.5, 61.88) * mm, v(-13.84, 61.88) * mm, v(-14.17, 61.96) * mm]});
            skFitSpline(sketch, "E306", {"points": [v(-42.85, 34.16) * mm, v(-42.6, 33.55) * mm, v(-42.66, 32.89) * mm, v(-42.57, 32.25) * mm]});
            skFitSpline(sketch, "E307", {"points": [v(-42.57, 32.25) * mm, v(-41.63, 25.4) * mm, v(-38.8, 19.57) * mm, v(-33.58, 15.04) * mm]});
            skFitSpline(sketch, "E308", {"points": [v(-33.58, 15.04) * mm, v(-30.64, 12.5) * mm, v(-27.24, 10.89) * mm, v(-23.4, 10.27) * mm]});
            skFitSpline(sketch, "E309", {"points": [v(-23.4, 10.27) * mm, v(-21.75, 10) * mm, v(-20.07, 10.08) * mm, v(-18.4, 10.01) * mm]});
            skFitSpline(sketch, "E310", {"points": [v(-18.4, 10.01) * mm, v(-17.32, 9.97) * mm, v(-16.24, 9.98) * mm, v(-15.16, 9.75) * mm]});
            skFitSpline(sketch, "E311", {"points": [v(-15.16, 9.75) * mm, v(-13.94, 9.5) * mm, v(-13.02, 8.84) * mm, v(-12.34, 7.82) * mm]});
            skFitSpline(sketch, "E312", {"points": [v(-12.34, 7.82) * mm, v(-12.12, 7.48) * mm, v(-11.9, 7.13) * mm, v(-11.74, 6.76) * mm]});
            skFitSpline(sketch, "E313", {"points": [v(-11.74, 6.76) * mm, v(-10.3, 3.3) * mm, v(-8.86, -0.17) * mm, v(-8.04, -3.86) * mm]});
            skFitSpline(sketch, "E314", {"points": [v(-8.04, -3.86) * mm, v(-7.85, -4.74) * mm, v(-7.75, -5.63) * mm, v(-7.8, -6.53) * mm]});
            skFitSpline(sketch, "E315", {"points": [v(-7.8, -6.53) * mm, v(-7.87, -7.98) * mm, v(-8.87, -8.66) * mm, v(-10.2, -8.17) * mm]});
            skFitSpline(sketch, "E316", {"points": [v(-10.2, -8.17) * mm, v(-10.5, -8.06) * mm, v(-10.77, -7.92) * mm, v(-11.11, -7.77) * mm]});
            skFitSpline(sketch, "E317", {"points": [v(-11.11, -7.77) * mm, v(-10.83, -8.76) * mm, v(-10.4, -9.55) * mm, v(-9.6, -10.14) * mm]});
            skFitSpline(sketch, "E318", {"points": [v(-9.6, -10.14) * mm, v(-8.24, -11.18) * mm, v(-6.68, -11.65) * mm, v(-5.02, -11.86) * mm]});
            skFitSpline(sketch, "E319", {"points": [v(-5.02, -11.86) * mm, v(-3.36, -12.08) * mm, v(-1.69, -12.11) * mm, v(-0.02, -12.17) * mm]});
            skFitSpline(sketch, "E320", {"points": [v(-0.02, -12.17) * mm, v(1.77, -12.22) * mm, v(3.54, -12.5) * mm, v(5.32, -12.72) * mm]});
            skFitSpline(sketch, "E321", {"points": [v(5.32, -12.72) * mm, v(8.35, -13.1) * mm, v(11.34, -13.75) * mm, v(14.36, -14.21) * mm]});
            skFitSpline(sketch, "E322", {"points": [v(14.36, -14.21) * mm, v(15.18, -14.34) * mm, v(15.97, -14.63) * mm, v(16.8, -14.73) * mm]});
            skFitSpline(sketch, "E323", {"points": [v(16.8, -14.73) * mm, v(16.9, -14.75) * mm, v(17.02, -14.82) * mm, v(17.01, -14.63) * mm]});
            skFitSpline(sketch, "E324", {"points": [v(17.01, -14.63) * mm, v(12.02, -12.4) * mm, v(7.75, -9.18) * mm, v(4.03, -5.13) * mm]});
            skFitSpline(sketch, "E325", {"points": [v(4.03, -5.13) * mm, v(2.16, -3.09) * mm, v(0.67, -0.8) * mm, v(-0.78, 1.53) * mm]});
            skFitSpline(sketch, "E326", {"points": [v(-0.78, 1.53) * mm, v(-4.46, 7.42) * mm, v(-6.77, 13.86) * mm, v(-8.17, 20.65) * mm]});
            skFitSpline(sketch, "E327", {"points": [v(-8.17, 20.65) * mm, v(-8.35, 21.53) * mm, v(-8.42, 22.43) * mm, v(-8.82, 23.24) * mm]});
            skFitSpline(sketch, "E328", {"points": [v(-8.82, 23.24) * mm, v(-9.7, 25.03) * mm, v(-11.2, 25.93) * mm, v(-13, 26.38) * mm]});
            skFitSpline(sketch, "E329", {"points": [v(-13, 26.38) * mm, v(-13.23, 26.44) * mm, v(-13.46, 26.48) * mm, v(-13.7, 26.5) * mm]});
            skFitSpline(sketch, "E330", {"points": [v(-13.7, 26.5) * mm, v(-14.73, 26.63) * mm, v(-15.75, 26.77) * mm, v(-16.72, 27.26) * mm]});
            skFitSpline(sketch, "E331", {"points": [v(-16.72, 27.26) * mm, v(-16.76, 26.85) * mm, v(-16.57, 26.54) * mm, v(-16.48, 26.2) * mm]});
            skFitSpline(sketch, "E332", {"points": [v(-16.48, 26.2) * mm, v(-16, 24.4) * mm, v(-15.74, 22.58) * mm, v(-16, 20.73) * mm]});
            skFitSpline(sketch, "E333", {"points": [v(-16, 20.73) * mm, v(-16.34, 18.26) * mm, v(-17.79, 16.82) * mm, v(-20.15, 16.25) * mm]});
            skFitSpline(sketch, "E334", {"points": [v(-20.15, 16.25) * mm, v(-23.4, 15.45) * mm, v(-26.44, 16.11) * mm, v(-29.3, 17.73) * mm]});
            skFitSpline(sketch, "E335", {"points": [v(-29.3, 17.73) * mm, v(-32.8, 19.7) * mm, v(-35.18, 22.74) * mm, v(-36.93, 26.32) * mm]});
            skFitSpline(sketch, "E336", {"points": [v(-36.93, 26.32) * mm, v(-38.65, 29.84) * mm, v(-39.63, 33.57) * mm, v(-39.2, 37.5) * mm]});
            skFitSpline(sketch, "E337", {"points": [v(-39.2, 37.5) * mm, v(-38.63, 42.7) * mm, v(-36.87, 47.38) * mm, v(-32.6, 50.7) * mm]});
            skFitSpline(sketch, "E338", {"points": [v(-32.6, 50.7) * mm, v(-31, 51.94) * mm, v(-29.21, 52.95) * mm, v(-27.17, 53.25) * mm]});
            skFitSpline(sketch, "E339", {"points": [v(-27.17, 53.25) * mm, v(-24.16, 53.7) * mm, v(-21.31, 53.26) * mm, v(-18.96, 51.14) * mm]});
            skFitSpline(sketch, "E340", {"points": [v(-18.96, 51.14) * mm, v(-17.44, 49.76) * mm, v(-17.08, 47.92) * mm, v(-17.36, 45.94) * mm]});
            skFitSpline(sketch, "E341", {"points": [v(-17.36, 45.94) * mm, v(-17.41, 45.6) * mm, v(-17.63, 45.32) * mm, v(-17.87, 45.07) * mm]});
            skFitSpline(sketch, "E342", {"points": [v(-17.87, 45.07) * mm, v(-18.18, 44.74) * mm, v(-18.5, 44.41) * mm, v(-18.82, 44.07) * mm]});
            skFitSpline(sketch, "E343", {"points": [v(-18.82, 44.07) * mm, v(-17.8, 43.58) * mm, v(-17.01, 42.78) * mm, v(-16.24, 41.96) * mm]});
            skFitSpline(sketch, "E344", {"points": [v(-16.24, 41.96) * mm, v(-15.3, 40.97) * mm, v(-14.34, 40.01) * mm, v(-13.2, 39.25) * mm]});
            skFitSpline(sketch, "E345", {"points": [v(-13.2, 39.25) * mm, v(-12.69, 38.9) * mm, v(-12.15, 38.94) * mm, v(-11.61, 38.96) * mm]});
            skFitSpline(sketch, "E346", {"points": [v(-11.61, 38.96) * mm, v(-11.36, 38.97) * mm, v(-11.24, 39.24) * mm, v(-11.12, 39.43) * mm]});
            skFitSpline(sketch, "E347", {"points": [v(-11.12, 39.43) * mm, v(-10.82, 39.9) * mm, v(-10.67, 40.43) * mm, v(-10.62, 40.96) * mm]});
            skFitSpline(sketch, "E348", {"points": [v(-10.62, 40.96) * mm, v(-10.29, 44.25) * mm, v(-10.66, 47.45) * mm, v(-11.87, 50.53) * mm]});
            skFitSpline(sketch, "E349", {"points": [v(-11.87, 50.53) * mm, v(-12.63, 52.45) * mm, v(-13.6, 54.26) * mm, v(-15, 55.8) * mm]});
            skFitSpline(sketch, "E350", {"points": [v(-15, 55.8) * mm, v(-16.53, 57.5) * mm, v(-18.38, 58.65) * mm, v(-20.61, 59.1) * mm]});
            skFitSpline(sketch, "E351", {"points": [v(-20.61, 59.1) * mm, v(-26.57, 60.31) * mm, v(-31.67, 58.5) * mm, v(-36.12, 54.5) * mm]});
            skFitSpline(sketch, "E352", {"points": [v(-36.12, 54.5) * mm, v(-38.56, 52.3) * mm, v(-39.83, 49.38) * mm, v(-40.94, 46.37) * mm]});
            skFitSpline(sketch, "E353", {"points": [v(-40.94, 46.37) * mm, v(-41.85, 43.9) * mm, v(-42.33, 41.33) * mm, v(-42.66, 38.73) * mm]});
            skFitSpline(sketch, "E354", {"points": [v(-42.66, 38.73) * mm, v(-42.7, 38.46) * mm, v(-42.67, 38.17) * mm, v(-42.85, 37.93) * mm]});
            skFitSpline(sketch, "E355", {"points": [v(-42.85, 36.81) * mm, v(-42.77, 36.37) * mm, v(-42.77, 35.93) * mm, v(-42.85, 35.49) * mm]});
            skFitSpline(sketch, "E356", {"points": [v(-42.85, 34.98) * mm, v(-42.8, 34.91) * mm, v(-42.8, 34.84) * mm, v(-42.85, 34.78) * mm]});
            skFitSpline(sketch, "E357", {"points": [v(40.63, -16.62) * mm, v(40.03, -16.65) * mm, v(39.42, -16.48) * mm, v(38.83, -16.7) * mm]});
            skFitSpline(sketch, "E358", {"points": [v(-42.85, 35.49) * mm, v(-42.69, 35.93) * mm, v(-42.69, 36.37) * mm, v(-42.85, 36.81) * mm]});
            skFitSpline(sketch, "E359", {"points": [v(-14.22, 61.96) * mm, v(-13.88, 61.8) * mm, v(-13.55, 61.8) * mm, v(-13.21, 61.96) * mm]});
            skFitSpline(sketch, "E360", {"points": [v(-42.85, 34.77) * mm, v(-42.7, 34.84) * mm, v(-42.72, 34.91) * mm, v(-42.85, 34.98) * mm]});
            skFitSpline(sketch, "E361", {"points": [v(36.2, -31.09) * mm, v(36.2, -31.19) * mm, v(36.14, -31.33) * mm, v(36.03, -31.52) * mm]});
            skFitSpline(sketch, "E362", {"points": [v(35.01, -30.98) * mm, v(34.51, -30.8) * mm, v(33.97, -30.7) * mm, v(33.37, -30.7) * mm]});
            skFitSpline(sketch, "E363", {"points": [v(27.52, -30.26) * mm, v(27.27, -29.84) * mm, v(27.06, -29.54) * mm, v(26.88, -29.35) * mm]});
            skFitSpline(sketch, "E364", {"points": [v(26.9, -29.28) * mm, v(26.91, -29.26) * mm, v(26.95, -29.22) * mm, v(27.02, -29.17) * mm]});
            skFitSpline(sketch, "E365", {"points": [v(27.02, -29.17) * mm, v(27.1, -29.12) * mm, v(27.16, -29.1) * mm, v(27.2, -29.1) * mm]});
            skFitSpline(sketch, "E366", {"points": [v(27.2, -29.1) * mm, v(27.32, -29.1) * mm, v(27.44, -29.17) * mm, v(27.55, -29.3) * mm]});
            skFitSpline(sketch, "E367", {"points": [v(27.55, -29.3) * mm, v(27.67, -29.44) * mm, v(27.78, -29.53) * mm, v(27.9, -29.57) * mm]});
            skFitSpline(sketch, "E368", {"points": [v(27.9, -29.57) * mm, v(28.63, -29.7) * mm, v(29.44, -29.76) * mm, v(30.32, -29.76) * mm]});
            skFitSpline(sketch, "E369", {"points": [v(34.41, -29.76) * mm, v(34.56, -29.76) * mm, v(34.8, -29.83) * mm, v(35.12, -29.97) * mm]});
            skFitSpline(sketch, "E370", {"points": [v(35.12, -29.97) * mm, v(35.46, -30.15) * mm, v(35.73, -30.31) * mm, v(35.93, -30.47) * mm]});
            skFitSpline(sketch, "E371", {"points": [v(35.93, -30.47) * mm, v(36.1, -30.6) * mm, v(36.2, -30.81) * mm, v(36.2, -31.09) * mm]});
            skFitSpline(sketch, "E372", {"points": [v(37.7, -29.32) * mm, v(38.17, -28.53) * mm, v(38.41, -27.65) * mm, v(38.41, -26.7) * mm]});
            skFitSpline(sketch, "E373", {"points": [v(38.41, -26.7) * mm, v(38.41, -26.04) * mm, v(38.22, -25.5) * mm, v(37.83, -25.09) * mm]});
            skFitSpline(sketch, "E374", {"points": [v(37.83, -25.09) * mm, v(37.44, -24.67) * mm, v(36.94, -24.4) * mm, v(36.33, -24.26) * mm]});
            skFitSpline(sketch, "E375", {"points": [v(36.33, -24.26) * mm, v(35.71, -24.13) * mm, v(34.95, -24.06) * mm, v(34.05, -24.06) * mm]});
            skFitSpline(sketch, "E376", {"points": [v(29.36, -24.3) * mm, v(28.94, -24.3) * mm, v(28.54, -24.31) * mm, v(28.15, -24.33) * mm]});
            skFitSpline(sketch, "E377", {"points": [v(28.15, -24.33) * mm, v(27.77, -24.35) * mm, v(27.48, -24.37) * mm, v(27.3, -24.39) * mm]});
            skFitSpline(sketch, "E378", {"points": [v(27.09, -23.13) * mm, v(28, -23.03) * mm, v(28.78, -22.97) * mm, v(29.45, -22.97) * mm]});
            skFitSpline(sketch, "E379", {"points": [v(36.14, -22.66) * mm, v(37.23, -22.66) * mm, v(38, -22.85) * mm, v(38.45, -23.23) * mm]});
            skFitSpline(sketch, "E380", {"points": [v(38.45, -23.23) * mm, v(38.93, -23.57) * mm, v(39.17, -24.28) * mm, v(39.17, -25.34) * mm]});
            skFitSpline(sketch, "E381", {"points": [v(39.17, -25.34) * mm, v(39.17, -26.27) * mm, v(39.07, -27.09) * mm, v(38.87, -27.8) * mm]});
            skFitSpline(sketch, "E382", {"points": [v(38.87, -27.8) * mm, v(38.67, -28.5) * mm, v(38.4, -29.07) * mm, v(38.04, -29.5) * mm]});
            skFitSpline(sketch, "E383", {"points": [v(41.6, -35.22) * mm, v(41.97, -35.64) * mm, v(42.27, -36.2) * mm, v(42.5, -36.9) * mm]});
            skFitSpline(sketch, "E384", {"points": [v(42.5, -36.9) * mm, v(42.74, -37.59) * mm, v(42.85, -38.1) * mm, v(42.85, -38.46) * mm]});
            skFitSpline(sketch, "E385", {"points": [v(42.85, -38.46) * mm, v(42.85, -39.3) * mm, v(42.5, -39.99) * mm, v(41.78, -40.53) * mm]});
            skFitSpline(sketch, "E386", {"points": [v(41.78, -40.53) * mm, v(41.06, -41.07) * mm, v(40, -41.34) * mm, v(38.6, -41.34) * mm]});
            skFitSpline(sketch, "E387", {"points": [v(38.6, -41.34) * mm, v(38.15, -41.34) * mm, v(37.7, -41.28) * mm, v(37.25, -41.15) * mm]});
            skFitSpline(sketch, "E388", {"points": [v(37.25, -41.15) * mm, v(36.8, -41.02) * mm, v(36.23, -40.79) * mm, v(35.56, -40.46) * mm]});
            skFitSpline(sketch, "E389", {"points": [v(35.56, -40.46) * mm, v(34.89, -40.13) * mm, v(34.18, -39.58) * mm, v(33.43, -38.82) * mm]});
            skFitSpline(sketch, "E390", {"points": [v(33.43, -38.82) * mm, v(32.68, -38.05) * mm, v(32.09, -37.3) * mm, v(31.65, -36.54) * mm]});
            skFitSpline(sketch, "E391", {"points": [v(31.65, -36.54) * mm, v(31.22, -35.8) * mm, v(30.9, -34.88) * mm, v(30.71, -33.8) * mm]});
            skFitSpline(sketch, "E392", {"points": [v(30.71, -33.8) * mm, v(30.52, -32.72) * mm, v(30.36, -31.52) * mm, v(30.25, -30.2) * mm]});
            skFitSpline(sketch, "E393", {"points": [v(29.88, -26.54) * mm, v(29.74, -25.38) * mm, v(29.63, -24.72) * mm, v(29.55, -24.56) * mm]});
            skFitSpline(sketch, "E394", {"points": [v(29.3, -24.3) * mm, v(29.2, -24.2) * mm, v(29.15, -24.15) * mm, v(29.13, -24.1) * mm]});
            skFitSpline(sketch, "E395", {"points": [v(29.13, -24.1) * mm, v(29.11, -24.07) * mm, v(29.1, -24.04) * mm, v(29.08, -24) * mm]});
            skFitSpline(sketch, "E396", {"points": [v(29.08, -24) * mm, v(29.12, -23.98) * mm, v(29.15, -23.96) * mm, v(29.18, -23.96) * mm]});
            skFitSpline(sketch, "E397", {"points": [v(29.55, -24.04) * mm, v(30.22, -24.23) * mm, v(30.7, -24.7) * mm, v(31.01, -25.46) * mm]});
            skFitSpline(sketch, "E398", {"points": [v(31.01, -25.46) * mm, v(31.32, -26.2) * mm, v(31.52, -26.85) * mm, v(31.61, -27.39) * mm]});
            skFitSpline(sketch, "E399", {"points": [v(31.61, -27.39) * mm, v(31.71, -27.92) * mm, v(31.76, -28.48) * mm, v(31.76, -29.06) * mm]});
            skFitSpline(sketch, "E400", {"points": [v(31.88, -31.82) * mm, v(31.88, -32.1) * mm, v(31.89, -32.36) * mm, v(31.92, -32.58) * mm]});
            skFitSpline(sketch, "E401", {"points": [v(31.92, -32.58) * mm, v(31.94, -32.8) * mm, v(32, -33.16) * mm, v(32.07, -33.64) * mm]});
            skFitSpline(sketch, "E402", {"points": [v(32.07, -33.64) * mm, v(32.15, -34.3) * mm, v(32.27, -34.99) * mm, v(32.45, -35.7) * mm]});
            skFitSpline(sketch, "E403", {"points": [v(32.45, -35.7) * mm, v(32.62, -36.42) * mm, v(32.86, -37.03) * mm, v(33.17, -37.52) * mm]});
            skFitSpline(sketch, "E404", {"points": [v(33.17, -37.52) * mm, v(33.47, -38.01) * mm, v(33.84, -38.43) * mm, v(34.26, -38.78) * mm]});
            skFitSpline(sketch, "E405", {"points": [v(34.26, -38.78) * mm, v(34.69, -39.09) * mm, v(35.16, -39.32) * mm, v(35.68, -39.48) * mm]});
            skFitSpline(sketch, "E406", {"points": [v(35.68, -39.48) * mm, v(36.2, -39.63) * mm, v(36.72, -39.71) * mm, v(37.27, -39.71) * mm]});
            skFitSpline(sketch, "E407", {"points": [v(38.3, -39.63) * mm, v(38.88, -39.54) * mm, v(39.37, -39.44) * mm, v(39.78, -39.32) * mm]});
            skFitSpline(sketch, "E408", {"points": [v(39.78, -39.32) * mm, v(40.19, -39.2) * mm, v(40.56, -39.06) * mm, v(40.88, -38.89) * mm]});
            skFitSpline(sketch, "E409", {"points": [v(40.88, -38.89) * mm, v(41.21, -38.72) * mm, v(41.47, -38.5) * mm, v(41.65, -38.22) * mm]});
            skFitSpline(sketch, "E410", {"points": [v(41.65, -38.22) * mm, v(41.83, -37.95) * mm, v(41.92, -37.64) * mm, v(41.92, -37.28) * mm]});
            skFitSpline(sketch, "E411", {"points": [v(41.92, -37.28) * mm, v(41.92, -37.03) * mm, v(41.88, -36.79) * mm, v(41.8, -36.55) * mm]});
            skFitSpline(sketch, "E412", {"points": [v(41.8, -36.55) * mm, v(41.73, -36.31) * mm, v(41.63, -36.11) * mm, v(41.52, -35.94) * mm]});
            skFitSpline(sketch, "E413", {"points": [v(41.52, -35.94) * mm, v(41.46, -35.83) * mm, v(41.42, -35.74) * mm, v(41.37, -35.68) * mm]});
            skFitSpline(sketch, "E414", {"points": [v(41.37, -35.68) * mm, v(41.32, -35.62) * mm, v(41.25, -35.53) * mm, v(41.15, -35.4) * mm]});
            skFitSpline(sketch, "E415", {"points": [v(40.72, -34.76) * mm, v(40.72, -34.65) * mm, v(40.78, -34.6) * mm, v(40.91, -34.6) * mm]});
            skFitSpline(sketch, "E416", {"points": [v(40.91, -34.6) * mm, v(41, -34.6) * mm, v(41.23, -34.8) * mm, v(41.6, -35.22) * mm]});
            skFitSpline(sketch, "E417", {"points": [v(24.15, -33.75) * mm, v(24.06, -33.18) * mm, v(23.87, -31.77) * mm, v(23.56, -29.53) * mm]});
            skFitSpline(sketch, "E418", {"points": [v(23.5, -28.89) * mm, v(23.5, -28.54) * mm, v(23.58, -28.37) * mm, v(23.75, -28.37) * mm]});
            skFitSpline(sketch, "E419", {"points": [v(23.75, -28.37) * mm, v(23.88, -28.37) * mm, v(24.04, -28.42) * mm, v(24.23, -28.54) * mm]});
            skFitSpline(sketch, "E420", {"points": [v(26.33, -30.01) * mm, v(26.43, -30.09) * mm, v(26.48, -30.19) * mm, v(26.48, -30.3) * mm]});
            skFitSpline(sketch, "E421", {"points": [v(26.17, -30.3) * mm, v(26.07, -30.28) * mm, v(25.91, -30.2) * mm, v(25.7, -30.04) * mm]});
            skFitSpline(sketch, "E422", {"points": [v(25.7, -30.04) * mm, v(25.49, -29.9) * mm, v(25.34, -29.82) * mm, v(25.26, -29.82) * mm]});
            skFitSpline(sketch, "E423", {"points": [v(25.26, -29.82) * mm, v(25.19, -29.82) * mm, v(25.15, -29.98) * mm, v(25.15, -30.3) * mm]});
            skFitSpline(sketch, "E424", {"points": [v(25.79, -35.64) * mm, v(25.8, -35.72) * mm, v(25.82, -35.8) * mm, v(25.83, -35.86) * mm]});
            skFitSpline(sketch, "E425", {"points": [v(25.83, -35.86) * mm, v(25.85, -35.93) * mm, v(25.87, -35.98) * mm, v(25.88, -36) * mm]});
            skFitSpline(sketch, "E426", {"points": [v(24.4, -35.44) * mm, v(24.32, -34.88) * mm, v(24.23, -34.32) * mm, v(24.15, -33.75) * mm]});
            skFitSpline(sketch, "E427", {"points": [v(21.46, -30.67) * mm, v(20.87, -29.75) * mm, v(20.57, -29.17) * mm, v(20.57, -28.93) * mm]});
            skFitSpline(sketch, "E428", {"points": [v(20.57, -28.93) * mm, v(20.57, -28.55) * mm, v(20.73, -28.37) * mm, v(21.05, -28.37) * mm]});
            skFitSpline(sketch, "E429", {"points": [v(21.05, -28.37) * mm, v(21.3, -28.37) * mm, v(21.63, -28.5) * mm, v(22.03, -28.76) * mm]});
            skFitSpline(sketch, "E430", {"points": [v(22.03, -28.76) * mm, v(22.44, -29.03) * mm, v(22.83, -29.4) * mm, v(23.19, -29.85) * mm]});
            skFitSpline(sketch, "E431", {"points": [v(23.89, -30.75) * mm, v(24.12, -30.85) * mm, v(24.23, -31.02) * mm, v(24.23, -31.25) * mm]});
            skFitSpline(sketch, "E432", {"points": [v(24.23, -31.25) * mm, v(24.23, -31.3) * mm, v(24.2, -31.35) * mm, v(24.14, -31.4) * mm]});
            skFitSpline(sketch, "E433", {"points": [v(24.14, -31.4) * mm, v(24.03, -31.4) * mm, v(23.87, -31.33) * mm, v(23.65, -31.18) * mm]});
            skFitSpline(sketch, "E434", {"points": [v(23.19, -30.77) * mm, v(22.74, -30.3) * mm, v(22.42, -30.07) * mm, v(22.24, -30.07) * mm]});
            skFitSpline(sketch, "E435", {"points": [v(22.24, -30.07) * mm, v(22.15, -30.07) * mm, v(22.1, -30.14) * mm, v(22.1, -30.27) * mm]});
            skFitSpline(sketch, "E436", {"points": [v(22.1, -30.27) * mm, v(22.1, -30.43) * mm, v(22.16, -30.68) * mm, v(22.27, -31) * mm]});
            skFitSpline(sketch, "E437", {"points": [v(22.27, -31) * mm, v(22.38, -31.33) * mm, v(22.44, -31.56) * mm, v(22.47, -31.7) * mm]});
            skFitSpline(sketch, "E438", {"points": [v(22.47, -31.7) * mm, v(22.5, -31.84) * mm, v(22.52, -31.96) * mm, v(22.53, -32.05) * mm]});
            skFitSpline(sketch, "E439", {"points": [v(22.53, -32.05) * mm, v(22.41, -32.05) * mm, v(22.06, -31.59) * mm, v(21.46, -30.67) * mm]});
            skFitSpline(sketch, "E440", {"points": [v(15.02, -29.33) * mm, v(14.92, -29.28) * mm, v(14.83, -29.19) * mm, v(14.76, -29.06) * mm]});
            skFitSpline(sketch, "E441", {"points": [v(14.76, -29.06) * mm, v(14.7, -28.94) * mm, v(14.65, -28.82) * mm, v(14.65, -28.72) * mm]});
            skFitSpline(sketch, "E442", {"points": [v(14.65, -28.72) * mm, v(14.65, -28.52) * mm, v(14.85, -28.42) * mm, v(15.24, -28.42) * mm]});
            skFitSpline(sketch, "E443", {"points": [v(16.71, -28.55) * mm, v(17.06, -28.55) * mm, v(17.39, -28.64) * mm, v(17.7, -28.8) * mm]});
            skFitSpline(sketch, "E444", {"points": [v(17.7, -28.8) * mm, v(18, -28.96) * mm, v(18.35, -29.24) * mm, v(18.73, -29.65) * mm]});
            skFitSpline(sketch, "E445", {"points": [v(18.73, -29.65) * mm, v(19.1, -30.06) * mm, v(19.4, -30.54) * mm, v(19.6, -31.09) * mm]});
            skFitSpline(sketch, "E446", {"points": [v(19.6, -31.09) * mm, v(19.8, -31.63) * mm, v(19.96, -32.08) * mm, v(20.05, -32.43) * mm]});
            skFitSpline(sketch, "E447", {"points": [v(20.05, -32.43) * mm, v(20.14, -32.78) * mm, v(20.2, -33.1) * mm, v(20.25, -33.38) * mm]});
            skFitSpline(sketch, "E448", {"points": [v(20.25, -33.38) * mm, v(20.3, -33.67) * mm, v(20.32, -33.9) * mm, v(20.34, -34.1) * mm]});
            skFitSpline(sketch, "E449", {"points": [v(20.34, -34.1) * mm, v(20.35, -34.28) * mm, v(20.36, -34.42) * mm, v(20.36, -34.5) * mm]});
            skFitSpline(sketch, "E450", {"points": [v(20.36, -34.5) * mm, v(20.36, -35.53) * mm, v(20.07, -36.04) * mm, v(19.5, -36.04) * mm]});
            skFitSpline(sketch, "E451", {"points": [v(19.5, -36.04) * mm, v(18.97, -36.04) * mm, v(18.24, -35.55) * mm, v(17.3, -34.56) * mm]});
            skFitSpline(sketch, "E452", {"points": [v(16.63, -33.84) * mm, v(16.43, -33.63) * mm, v(16.26, -33.42) * mm, v(16.13, -33.2) * mm]});
            skFitSpline(sketch, "E453", {"points": [v(16.13, -33.2) * mm, v(16, -32.97) * mm, v(15.93, -32.75) * mm, v(15.93, -32.53) * mm]});
            skFitSpline(sketch, "E454", {"points": [v(15.93, -32.53) * mm, v(15.93, -32.47) * mm, v(15.96, -32.39) * mm, v(16.01, -32.3) * mm]});
            skFitSpline(sketch, "E455", {"points": [v(16.46, -32.84) * mm, v(16.73, -33.22) * mm, v(17.05, -33.61) * mm, v(17.43, -34) * mm]});
            skFitSpline(sketch, "E456", {"points": [v(17.43, -34) * mm, v(17.8, -34.4) * mm, v(18.13, -34.6) * mm, v(18.4, -34.6) * mm]});
            skFitSpline(sketch, "E457", {"points": [v(18.4, -34.6) * mm, v(18.72, -34.6) * mm, v(18.88, -34.26) * mm, v(18.88, -33.58) * mm]});
            skFitSpline(sketch, "E458", {"points": [v(18.88, -33.58) * mm, v(18.88, -33.1) * mm, v(18.81, -32.5) * mm, v(18.68, -31.8) * mm]});
            skFitSpline(sketch, "E459", {"points": [v(18.68, -31.8) * mm, v(18.54, -31.1) * mm, v(18.39, -30.58) * mm, v(18.21, -30.24) * mm]});
            skFitSpline(sketch, "E460", {"points": [v(18.21, -30.24) * mm, v(18.04, -29.9) * mm, v(17.85, -29.68) * mm, v(17.65, -29.57) * mm]});
            skFitSpline(sketch, "E461", {"points": [v(17.65, -29.57) * mm, v(17.45, -29.46) * mm, v(17.22, -29.4) * mm, v(16.96, -29.4) * mm]});
            skFitSpline(sketch, "E462", {"points": [v(14.54, -29.14) * mm, v(14.54, -28.69) * mm, v(14.68, -28.46) * mm, v(14.97, -28.46) * mm]});
            skFitSpline(sketch, "E463", {"points": [v(14.97, -28.46) * mm, v(15.12, -28.46) * mm, v(15.3, -28.55) * mm, v(15.53, -28.73) * mm]});
            skFitSpline(sketch, "E464", {"points": [v(15.53, -28.73) * mm, v(15.72, -28.93) * mm, v(15.88, -29.18) * mm, v(16, -29.48) * mm]});
            skFitSpline(sketch, "E465", {"points": [v(16, -29.48) * mm, v(16.12, -29.78) * mm, v(16.2, -30.05) * mm, v(16.26, -30.28) * mm]});
            skFitSpline(sketch, "E466", {"points": [v(16.26, -30.28) * mm, v(16.31, -30.5) * mm, v(16.35, -30.78) * mm, v(16.38, -31.1) * mm]});
            skFitSpline(sketch, "E467", {"points": [v(16.85, -35.3) * mm, v(16.85, -35.79) * mm, v(16.74, -36.03) * mm, v(16.52, -36.03) * mm]});
            skFitSpline(sketch, "E468", {"points": [v(16.52, -36.03) * mm, v(16.3, -36.03) * mm, v(16.02, -35.88) * mm, v(15.66, -35.6) * mm]});
            skFitSpline(sketch, "E469", {"points": [v(15.66, -35.6) * mm, v(15.3, -35.35) * mm, v(14.71, -34.87) * mm, v(13.9, -34.14) * mm]});
            skFitSpline(sketch, "E470", {"points": [v(13.9, -34.14) * mm, v(13.85, -34.08) * mm, v(13.8, -34.03) * mm, v(13.78, -33.99) * mm]});
            skFitSpline(sketch, "E471", {"points": [v(13.78, -33.99) * mm, v(13.76, -33.95) * mm, v(13.74, -33.91) * mm, v(13.72, -33.87) * mm]});
            skFitSpline(sketch, "E472", {"points": [v(13.72, -33.87) * mm, v(13.72, -33.85) * mm, v(13.76, -33.81) * mm, v(13.82, -33.78) * mm]});
            skFitSpline(sketch, "E473", {"points": [v(13.82, -33.78) * mm, v(13.91, -33.78) * mm, v(14.02, -33.82) * mm, v(14.16, -33.91) * mm]});
            skFitSpline(sketch, "E474", {"points": [v(14.16, -33.91) * mm, v(14.3, -34) * mm, v(14.42, -34.1) * mm, v(14.54, -34.18) * mm]});
            skFitSpline(sketch, "E475", {"points": [v(14.54, -34.18) * mm, v(14.65, -34.27) * mm, v(14.76, -34.36) * mm, v(14.85, -34.45) * mm]});
            skFitSpline(sketch, "E476", {"points": [v(15.26, -34.75) * mm, v(15.27, -34.73) * mm, v(15.28, -34.71) * mm, v(15.3, -34.68) * mm]});
            skFitSpline(sketch, "E477", {"points": [v(15.3, -34.68) * mm, v(15.32, -34.65) * mm, v(15.33, -34.6) * mm, v(15.33, -34.51) * mm]});
            skFitSpline(sketch, "E478", {"points": [v(8.27, -29.31) * mm, v(8.17, -29.25) * mm, v(8.1, -29.17) * mm, v(8.04, -29.08) * mm]});
            skFitSpline(sketch, "E479", {"points": [v(7.89, -28.74) * mm, v(7.89, -28.55) * mm, v(8.08, -28.46) * mm, v(8.47, -28.35) * mm]});
            skFitSpline(sketch, "E480", {"points": [v(10.14, -28.6) * mm, v(10.8, -28.66) * mm, v(11.4, -28.9) * mm, v(11.9, -29.32) * mm]});
            skFitSpline(sketch, "E481", {"points": [v(11.9, -29.32) * mm, v(12.39, -29.73) * mm, v(12.8, -30.26) * mm, v(13.12, -30.9) * mm]});
            skFitSpline(sketch, "E482", {"points": [v(13.12, -30.9) * mm, v(13.45, -31.53) * mm, v(13.66, -32.18) * mm, v(13.76, -32.84) * mm]});
            skFitSpline(sketch, "E483", {"points": [v(13.76, -32.84) * mm, v(13.87, -33.5) * mm, v(13.92, -34.06) * mm, v(13.92, -34.53) * mm]});
            skFitSpline(sketch, "E484", {"points": [v(13.92, -34.53) * mm, v(13.92, -35.58) * mm, v(13.67, -36.1) * mm, v(13.16, -36.1) * mm]});
            skFitSpline(sketch, "E485", {"points": [v(13.16, -36.1) * mm, v(12.73, -36.1) * mm, v(12.1, -35.65) * mm, v(11.28, -34.74) * mm]});
            skFitSpline(sketch, "E486", {"points": [v(10.47, -33.88) * mm, v(10.2, -33.6) * mm, v(10.01, -33.4) * mm, v(9.88, -33.26) * mm]});
            skFitSpline(sketch, "E487", {"points": [v(9.88, -33.26) * mm, v(9.75, -33.12) * mm, v(9.62, -32.94) * mm, v(9.49, -32.74) * mm]});
            skFitSpline(sketch, "E488", {"points": [v(9.49, -32.74) * mm, v(9.35, -32.54) * mm, v(9.28, -32.33) * mm, v(9.28, -32.1) * mm]});
            skFitSpline(sketch, "E489", {"points": [v(9.28, -32.1) * mm, v(9.28, -31.93) * mm, v(9.32, -31.84) * mm, v(9.4, -31.84) * mm]});
            skFitSpline(sketch, "E490", {"points": [v(9.4, -31.84) * mm, v(9.48, -31.84) * mm, v(9.57, -31.9) * mm, v(9.69, -32.05) * mm]});
            skFitSpline(sketch, "E491", {"points": [v(11.14, -33.94) * mm, v(11.65, -34.48) * mm, v(12.02, -34.75) * mm, v(12.27, -34.75) * mm]});
            skFitSpline(sketch, "E492", {"points": [v(12.27, -34.75) * mm, v(12.49, -34.75) * mm, v(12.6, -34.54) * mm, v(12.6, -34.13) * mm]});
            skFitSpline(sketch, "E493", {"points": [v(12.13, -31.6) * mm, v(12.02, -31.02) * mm, v(11.87, -30.55) * mm, v(11.68, -30.21) * mm]});
            skFitSpline(sketch, "E494", {"points": [v(11.68, -30.21) * mm, v(11.5, -29.87) * mm, v(11.29, -29.65) * mm, v(11.07, -29.55) * mm]});
            skFitSpline(sketch, "E495", {"points": [v(11.07, -29.55) * mm, v(10.85, -29.44) * mm, v(10.6, -29.4) * mm, v(10.33, -29.4) * mm]});
            skFitSpline(sketch, "E496", {"points": [v(8.7, -28.7) * mm, v(8.82, -28.7) * mm, v(8.99, -28.7) * mm, v(9.2, -28.7) * mm]});
            skFitSpline(sketch, "E497", {"points": [v(9.2, -28.7) * mm, v(9.37, -28.7) * mm, v(9.46, -28.75) * mm, v(9.46, -28.84) * mm]});
            skFitSpline(sketch, "E498", {"points": [v(10.47, -37.68) * mm, v(10.47, -38.03) * mm, v(10.49, -38.32) * mm, v(10.52, -38.56) * mm]});
            skFitSpline(sketch, "E499", {"points": [v(10.52, -38.56) * mm, v(10.56, -38.8) * mm, v(10.61, -39.05) * mm, v(10.68, -39.3) * mm]});
            skFitSpline(sketch, "E500", {"points": [v(10.68, -39.3) * mm, v(10.78, -39.59) * mm, v(10.95, -39.8) * mm, v(11.18, -39.95) * mm]});
            skFitSpline(sketch, "E501", {"points": [v(11.18, -39.95) * mm, v(11.44, -40.14) * mm, v(11.82, -40.24) * mm, v(12.3, -40.24) * mm]});
            skFitSpline(sketch, "E502", {"points": [v(12.3, -40.24) * mm, v(12.8, -40.24) * mm, v(13.23, -40.1) * mm, v(13.6, -39.8) * mm]});
            skFitSpline(sketch, "E503", {"points": [v(13.6, -39.8) * mm, v(13.97, -39.51) * mm, v(14.15, -39.17) * mm, v(14.15, -38.79) * mm]});
            skFitSpline(sketch, "E504", {"points": [v(14.15, -38.79) * mm, v(14.15, -38.63) * mm, v(14.09, -38.42) * mm, v(13.97, -38.16) * mm]});
            skFitSpline(sketch, "E505", {"points": [v(13.97, -38.16) * mm, v(13.84, -37.9) * mm, v(13.64, -37.65) * mm, v(13.36, -37.43) * mm]});
            skFitSpline(sketch, "E506", {"points": [v(13.36, -37.43) * mm, v(13.09, -37.2) * mm, v(12.88, -37.06) * mm, v(12.75, -36.97) * mm]});
            skFitSpline(sketch, "E507", {"points": [v(12.75, -36.97) * mm, v(12.63, -36.89) * mm, v(12.46, -36.8) * mm, v(12.25, -36.7) * mm]});
            skFitSpline(sketch, "E508", {"points": [v(11.22, -36.28) * mm, v(11.05, -36.22) * mm, v(10.93, -36.17) * mm, v(10.85, -36.13) * mm]});
            skFitSpline(sketch, "E509", {"points": [v(10.85, -36.13) * mm, v(10.78, -36.1) * mm, v(10.71, -36.05) * mm, v(10.66, -36) * mm]});
            skFitSpline(sketch, "E510", {"points": [v(10.7, -35.94) * mm, v(10.92, -35.94) * mm, v(11.3, -36.06) * mm, v(11.84, -36.3) * mm]});
            skFitSpline(sketch, "E511", {"points": [v(11.84, -36.3) * mm, v(12.39, -36.55) * mm, v(12.92, -36.85) * mm, v(13.44, -37.22) * mm]});
            skFitSpline(sketch, "E512", {"points": [v(13.44, -37.22) * mm, v(13.97, -37.58) * mm, v(14.33, -37.93) * mm, v(14.53, -38.26) * mm]});
            skFitSpline(sketch, "E513", {"points": [v(14.53, -38.26) * mm, v(14.73, -38.6) * mm, v(14.83, -39.01) * mm, v(14.83, -39.5) * mm]});
            skFitSpline(sketch, "E514", {"points": [v(14.83, -39.5) * mm, v(14.83, -40) * mm, v(14.68, -40.42) * mm, v(14.4, -40.78) * mm]});
            skFitSpline(sketch, "E515", {"points": [v(14.4, -40.78) * mm, v(14.1, -41.15) * mm, v(13.7, -41.33) * mm, v(13.16, -41.33) * mm]});
            skFitSpline(sketch, "E516", {"points": [v(13.16, -41.33) * mm, v(12.49, -41.33) * mm, v(11.78, -41.05) * mm, v(11.02, -40.5) * mm]});
            skFitSpline(sketch, "E517", {"points": [v(11.02, -40.5) * mm, v(10.26, -39.94) * mm, v(9.75, -39.25) * mm, v(9.49, -38.43) * mm]});
            skFitSpline(sketch, "E518", {"points": [v(9.49, -38.43) * mm, v(9.22, -37.6) * mm, v(9.02, -36.56) * mm, v(8.88, -35.3) * mm]});
            skFitSpline(sketch, "E519", {"points": [v(8.5, -31.75) * mm, v(8.4, -30.62) * mm, v(8.24, -29.7) * mm, v(8.04, -28.95) * mm]});
            skFitSpline(sketch, "E520", {"points": [v(8.04, -28.95) * mm, v(8.04, -28.79) * mm, v(8.26, -28.7) * mm, v(8.7, -28.7) * mm]});
            skFitSpline(sketch, "E521", {"points": [v(2.67, -29.33) * mm, v(2.57, -29.28) * mm, v(2.48, -29.19) * mm, v(2.4, -29.06) * mm]});
            skFitSpline(sketch, "E522", {"points": [v(2.4, -29.06) * mm, v(2.34, -28.94) * mm, v(2.3, -28.82) * mm, v(2.3, -28.72) * mm]});
            skFitSpline(sketch, "E523", {"points": [v(2.3, -28.72) * mm, v(2.3, -28.52) * mm, v(2.5, -28.42) * mm, v(2.88, -28.42) * mm]});
            skFitSpline(sketch, "E524", {"points": [v(4.36, -28.55) * mm, v(4.7, -28.55) * mm, v(5.04, -28.64) * mm, v(5.35, -28.8) * mm]});
            skFitSpline(sketch, "E525", {"points": [v(5.35, -28.8) * mm, v(5.66, -28.96) * mm, v(6, -29.24) * mm, v(6.37, -29.65) * mm]});
            skFitSpline(sketch, "E526", {"points": [v(6.37, -29.65) * mm, v(6.75, -30.06) * mm, v(7.04, -30.54) * mm, v(7.25, -31.09) * mm]});
            skFitSpline(sketch, "E527", {"points": [v(7.25, -31.09) * mm, v(7.45, -31.63) * mm, v(7.6, -32.08) * mm, v(7.7, -32.43) * mm]});
            skFitSpline(sketch, "E528", {"points": [v(7.7, -32.43) * mm, v(7.78, -32.78) * mm, v(7.85, -33.1) * mm, v(7.9, -33.38) * mm]});
            skFitSpline(sketch, "E529", {"points": [v(7.9, -33.38) * mm, v(7.94, -33.67) * mm, v(7.97, -33.9) * mm, v(7.98, -34.1) * mm]});
            skFitSpline(sketch, "E530", {"points": [v(7.98, -34.1) * mm, v(8, -34.28) * mm, v(8, -34.42) * mm, v(8, -34.5) * mm]});
            skFitSpline(sketch, "E531", {"points": [v(8, -34.5) * mm, v(8, -35.53) * mm, v(7.72, -36.04) * mm, v(7.15, -36.04) * mm]});
            skFitSpline(sketch, "E532", {"points": [v(7.15, -36.04) * mm, v(6.62, -36.04) * mm, v(5.88, -35.55) * mm, v(4.94, -34.56) * mm]});
            skFitSpline(sketch, "E533", {"points": [v(4.28, -33.84) * mm, v(4.07, -33.63) * mm, v(3.9, -33.42) * mm, v(3.78, -33.2) * mm]});
            skFitSpline(sketch, "E534", {"points": [v(3.78, -33.2) * mm, v(3.65, -32.97) * mm, v(3.58, -32.75) * mm, v(3.58, -32.53) * mm]});
            skFitSpline(sketch, "E535", {"points": [v(3.58, -32.53) * mm, v(3.58, -32.47) * mm, v(3.6, -32.39) * mm, v(3.66, -32.3) * mm]});
            skFitSpline(sketch, "E536", {"points": [v(4.1, -32.84) * mm, v(4.38, -33.22) * mm, v(4.7, -33.61) * mm, v(5.07, -34) * mm]});
            skFitSpline(sketch, "E537", {"points": [v(5.07, -34) * mm, v(5.45, -34.4) * mm, v(5.77, -34.6) * mm, v(6.04, -34.6) * mm]});
            skFitSpline(sketch, "E538", {"points": [v(6.04, -34.6) * mm, v(6.37, -34.6) * mm, v(6.53, -34.26) * mm, v(6.53, -33.58) * mm]});
            skFitSpline(sketch, "E539", {"points": [v(6.53, -33.58) * mm, v(6.53, -33.1) * mm, v(6.46, -32.5) * mm, v(6.33, -31.8) * mm]});
            skFitSpline(sketch, "E540", {"points": [v(6.33, -31.8) * mm, v(6.19, -31.1) * mm, v(6.03, -30.58) * mm, v(5.86, -30.24) * mm]});
            skFitSpline(sketch, "E541", {"points": [v(5.86, -30.24) * mm, v(5.69, -29.9) * mm, v(5.5, -29.68) * mm, v(5.3, -29.57) * mm]});
            skFitSpline(sketch, "E542", {"points": [v(5.3, -29.57) * mm, v(5.1, -29.46) * mm, v(4.87, -29.4) * mm, v(4.6, -29.4) * mm]});
            skFitSpline(sketch, "E543", {"points": [v(2.19, -29.14) * mm, v(2.19, -28.69) * mm, v(2.33, -28.46) * mm, v(2.62, -28.46) * mm]});
            skFitSpline(sketch, "E544", {"points": [v(2.62, -28.46) * mm, v(2.77, -28.46) * mm, v(2.96, -28.55) * mm, v(3.17, -28.73) * mm]});
            skFitSpline(sketch, "E545", {"points": [v(3.17, -28.73) * mm, v(3.37, -28.93) * mm, v(3.52, -29.18) * mm, v(3.65, -29.48) * mm]});
            skFitSpline(sketch, "E546", {"points": [v(3.65, -29.48) * mm, v(3.77, -29.78) * mm, v(3.86, -30.05) * mm, v(3.9, -30.28) * mm]});
            skFitSpline(sketch, "E547", {"points": [v(3.9, -30.28) * mm, v(3.96, -30.5) * mm, v(4, -30.78) * mm, v(4.02, -31.1) * mm]});
            skFitSpline(sketch, "E548", {"points": [v(4.5, -35.3) * mm, v(4.5, -35.79) * mm, v(4.38, -36.03) * mm, v(4.16, -36.03) * mm]});
            skFitSpline(sketch, "E549", {"points": [v(4.16, -36.03) * mm, v(3.96, -36.03) * mm, v(3.67, -35.88) * mm, v(3.3, -35.6) * mm]});
            skFitSpline(sketch, "E550", {"points": [v(3.3, -35.6) * mm, v(2.95, -35.35) * mm, v(2.36, -34.87) * mm, v(1.54, -34.14) * mm]});
            skFitSpline(sketch, "E551", {"points": [v(1.54, -34.14) * mm, v(1.5, -34.08) * mm, v(1.45, -34.03) * mm, v(1.43, -33.99) * mm]});
            skFitSpline(sketch, "E552", {"points": [v(1.43, -33.99) * mm, v(1.4, -33.95) * mm, v(1.38, -33.91) * mm, v(1.37, -33.87) * mm]});
            skFitSpline(sketch, "E553", {"points": [v(1.37, -33.87) * mm, v(1.37, -33.85) * mm, v(1.4, -33.81) * mm, v(1.47, -33.78) * mm]});
            skFitSpline(sketch, "E554", {"points": [v(1.47, -33.78) * mm, v(1.56, -33.78) * mm, v(1.67, -33.82) * mm, v(1.8, -33.91) * mm]});
            skFitSpline(sketch, "E555", {"points": [v(1.8, -33.91) * mm, v(1.94, -34) * mm, v(2.07, -34.1) * mm, v(2.18, -34.18) * mm]});
            skFitSpline(sketch, "E556", {"points": [v(2.18, -34.18) * mm, v(2.3, -34.27) * mm, v(2.4, -34.36) * mm, v(2.5, -34.45) * mm]});
            skFitSpline(sketch, "E557", {"points": [v(2.9, -34.75) * mm, v(2.92, -34.73) * mm, v(2.93, -34.71) * mm, v(2.95, -34.68) * mm]});
            skFitSpline(sketch, "E558", {"points": [v(2.95, -34.68) * mm, v(2.97, -34.65) * mm, v(2.98, -34.6) * mm, v(2.98, -34.51) * mm]});
            skFitSpline(sketch, "E559", {"points": [v(0.84, -30.58) * mm, v(0.58, -30.28) * mm, v(0.36, -30.13) * mm, v(0.17, -30.13) * mm]});
            skFitSpline(sketch, "E560", {"points": [v(0.17, -30.13) * mm, v(0.01, -30.13) * mm, v(-0.07, -30.34) * mm, v(-0.07, -30.77) * mm]});
            skFitSpline(sketch, "E561", {"points": [v(0.85, -37.11) * mm, v(1.16, -38.88) * mm, v(1.31, -40.07) * mm, v(1.31, -40.66) * mm]});
            skFitSpline(sketch, "E562", {"points": [v(1.31, -40.66) * mm, v(1.31, -41.15) * mm, v(1.2, -41.4) * mm, v(0.96, -41.4) * mm]});
            skFitSpline(sketch, "E563", {"points": [v(0.32, -41.16) * mm, v(0.12, -41.06) * mm, v(-0.05, -40.98) * mm, v(-0.17, -40.93) * mm]});
            skFitSpline(sketch, "E564", {"points": [v(-0.17, -40.93) * mm, v(-0.3, -40.88) * mm, v(-0.44, -40.82) * mm, v(-0.6, -40.76) * mm]});
            skFitSpline(sketch, "E565", {"points": [v(-0.6, -40.76) * mm, v(-0.78, -40.7) * mm, v(-1.03, -40.66) * mm, v(-1.36, -40.66) * mm]});
            skFitSpline(sketch, "E566", {"points": [v(-1.36, -40.66) * mm, v(-1.61, -40.66) * mm, v(-1.73, -40.49) * mm, v(-1.73, -40.14) * mm]});
            skFitSpline(sketch, "E567", {"points": [v(-1.73, -40.14) * mm, v(-1.73, -39.9) * mm, v(-1.62, -39.79) * mm, v(-1.4, -39.79) * mm]});
            skFitSpline(sketch, "E568", {"points": [v(-1.4, -39.79) * mm, v(-1, -40.03) * mm, v(-0.75, -40.16) * mm, v(-0.65, -40.16) * mm]});
            skFitSpline(sketch, "E569", {"points": [v(-0.65, -40.16) * mm, v(-0.5, -40.16) * mm, v(-0.43, -40) * mm, v(-0.43, -39.67) * mm]});
            skFitSpline(sketch, "E570", {"points": [v(-1.62, -29.37) * mm, v(-1.62, -28.8) * mm, v(-1.5, -28.52) * mm, v(-1.25, -28.52) * mm]});
            skFitSpline(sketch, "E571", {"points": [v(-1.25, -28.52) * mm, v(-0.9, -28.52) * mm, v(-0.36, -28.87) * mm, v(0.38, -29.58) * mm]});
            skFitSpline(sketch, "E572", {"points": [v(0.38, -29.58) * mm, v(1.12, -30.28) * mm, v(1.49, -30.7) * mm, v(1.49, -30.85) * mm]});
            skFitSpline(sketch, "E573", {"points": [v(1.49, -30.85) * mm, v(1.49, -30.96) * mm, v(1.44, -31.02) * mm, v(1.35, -31.02) * mm]});
            skFitSpline(sketch, "E574", {"points": [v(1.35, -31.02) * mm, v(1.26, -31.02) * mm, v(1.09, -30.87) * mm, v(0.84, -30.58) * mm]});
            skFitSpline(sketch, "E575", {"points": [v(-0.94, -35.28) * mm, v(-0.83, -35.19) * mm, v(-0.72, -35.14) * mm, v(-0.6, -35.14) * mm]});
            skFitSpline(sketch, "E576", {"points": [v(-0.6, -35.14) * mm, v(-0.53, -35.15) * mm, v(-0.48, -35.19) * mm, v(-0.45, -35.24) * mm]});
            skFitSpline(sketch, "E577", {"points": [v(-0.45, -35.24) * mm, v(-0.43, -35.3) * mm, v(-0.41, -35.36) * mm, v(-0.41, -35.45) * mm]});
            skFitSpline(sketch, "E578", {"points": [v(-0.36, -35.65) * mm, v(-0.24, -35.85) * mm, v(-0.18, -36) * mm, v(-0.18, -36.1) * mm]});
            skFitSpline(sketch, "E579", {"points": [v(-2.27, -36.11) * mm, v(-3.28, -36.11) * mm, v(-3.98, -35.64) * mm, v(-4.35, -34.7) * mm]});
            skFitSpline(sketch, "E580", {"points": [v(-4.35, -34.7) * mm, v(-4.72, -33.76) * mm, v(-4.97, -32.87) * mm, v(-5.1, -32.03) * mm]});
            skFitSpline(sketch, "E581", {"points": [v(-5.1, -32.03) * mm, v(-5.24, -31.2) * mm, v(-5.3, -30.66) * mm, v(-5.32, -30.45) * mm]});
            skFitSpline(sketch, "E582", {"points": [v(-5.32, -30.45) * mm, v(-5.33, -30.24) * mm, v(-5.34, -30.04) * mm, v(-5.34, -29.84) * mm]});
            skFitSpline(sketch, "E583", {"points": [v(-5.34, -29.84) * mm, v(-5.34, -28.94) * mm, v(-5.11, -28.49) * mm, v(-4.66, -28.49) * mm]});
            skFitSpline(sketch, "E584", {"points": [v(-4.66, -28.49) * mm, v(-4.2, -28.49) * mm, v(-3.5, -29) * mm, v(-2.53, -30.03) * mm]});
            skFitSpline(sketch, "E585", {"points": [v(-1.85, -30.67) * mm, v(-1.51, -30.98) * mm, v(-1.27, -31.23) * mm, v(-1.13, -31.41) * mm]});
            skFitSpline(sketch, "E586", {"points": [v(-1.13, -31.41) * mm, v(-0.99, -31.6) * mm, v(-0.92, -31.79) * mm, v(-0.92, -32) * mm]});
            skFitSpline(sketch, "E587", {"points": [v(-0.92, -32) * mm, v(-0.92, -32.05) * mm, v(-0.95, -32.1) * mm, v(-1.02, -32.17) * mm]});
            skFitSpline(sketch, "E588", {"points": [v(-1.02, -32.17) * mm, v(-1.18, -32.17) * mm, v(-1.58, -31.8) * mm, v(-2.22, -31.05) * mm]});
            skFitSpline(sketch, "E589", {"points": [v(-2.22, -31.05) * mm, v(-2.76, -30.47) * mm, v(-3.17, -30.18) * mm, v(-3.44, -30.18) * mm]});
            skFitSpline(sketch, "E590", {"points": [v(-3.44, -30.18) * mm, v(-3.72, -30.18) * mm, v(-3.87, -30.47) * mm, v(-3.87, -31.07) * mm]});
            skFitSpline(sketch, "E591", {"points": [v(-3.87, -31.07) * mm, v(-3.87, -31.6) * mm, v(-3.78, -32.28) * mm, v(-3.6, -33.1) * mm]});
            skFitSpline(sketch, "E592", {"points": [v(-3.6, -33.1) * mm, v(-3.43, -33.93) * mm, v(-3.2, -34.56) * mm, v(-2.94, -35) * mm]});
            skFitSpline(sketch, "E593", {"points": [v(-2.94, -35) * mm, v(-2.68, -35.43) * mm, v(-2.37, -35.65) * mm, v(-2, -35.65) * mm]});
            skFitSpline(sketch, "E594", {"points": [v(-2, -35.65) * mm, v(-1.7, -35.65) * mm, v(-1.34, -35.52) * mm, v(-0.94, -35.28) * mm]});
            skFitSpline(sketch, "E595", {"points": [v(-10.8, -29.33) * mm, v(-10.91, -29.28) * mm, v(-11, -29.19) * mm, v(-11.07, -29.06) * mm]});
            skFitSpline(sketch, "E596", {"points": [v(-11.07, -29.06) * mm, v(-11.14, -28.94) * mm, v(-11.18, -28.82) * mm, v(-11.18, -28.72) * mm]});
            skFitSpline(sketch, "E597", {"points": [v(-11.18, -28.72) * mm, v(-11.18, -28.52) * mm, v(-10.98, -28.42) * mm, v(-10.6, -28.42) * mm]});
            skFitSpline(sketch, "E598", {"points": [v(-9.12, -28.55) * mm, v(-8.77, -28.55) * mm, v(-8.44, -28.64) * mm, v(-8.13, -28.8) * mm]});
            skFitSpline(sketch, "E599", {"points": [v(-8.13, -28.8) * mm, v(-7.82, -28.96) * mm, v(-7.48, -29.24) * mm, v(-7.1, -29.65) * mm]});
            skFitSpline(sketch, "E600", {"points": [v(-7.1, -29.65) * mm, v(-6.73, -30.06) * mm, v(-6.44, -30.54) * mm, v(-6.23, -31.09) * mm]});
            skFitSpline(sketch, "E601", {"points": [v(-6.23, -31.09) * mm, v(-6.03, -31.63) * mm, v(-5.88, -32.08) * mm, v(-5.79, -32.43) * mm]});
            skFitSpline(sketch, "E602", {"points": [v(-5.79, -32.43) * mm, v(-5.7, -32.78) * mm, v(-5.63, -33.1) * mm, v(-5.58, -33.38) * mm]});
            skFitSpline(sketch, "E603", {"points": [v(-5.58, -33.38) * mm, v(-5.54, -33.67) * mm, v(-5.5, -33.9) * mm, v(-5.5, -34.1) * mm]});
            skFitSpline(sketch, "E604", {"points": [v(-5.5, -34.1) * mm, v(-5.48, -34.28) * mm, v(-5.48, -34.42) * mm, v(-5.48, -34.5) * mm]});
            skFitSpline(sketch, "E605", {"points": [v(-5.48, -34.5) * mm, v(-5.48, -35.53) * mm, v(-5.76, -36.04) * mm, v(-6.33, -36.04) * mm]});
            skFitSpline(sketch, "E606", {"points": [v(-6.33, -36.04) * mm, v(-6.86, -36.04) * mm, v(-7.6, -35.55) * mm, v(-8.54, -34.56) * mm]});
            skFitSpline(sketch, "E607", {"points": [v(-9.2, -33.84) * mm, v(-9.4, -33.63) * mm, v(-9.57, -33.42) * mm, v(-9.7, -33.2) * mm]});
            skFitSpline(sketch, "E608", {"points": [v(-9.7, -33.2) * mm, v(-9.83, -32.97) * mm, v(-9.9, -32.75) * mm, v(-9.9, -32.53) * mm]});
            skFitSpline(sketch, "E609", {"points": [v(-9.9, -32.53) * mm, v(-9.9, -32.47) * mm, v(-9.87, -32.39) * mm, v(-9.82, -32.3) * mm]});
            skFitSpline(sketch, "E610", {"points": [v(-9.37, -32.84) * mm, v(-9.1, -33.22) * mm, v(-8.78, -33.61) * mm, v(-8.4, -34) * mm]});
            skFitSpline(sketch, "E611", {"points": [v(-8.4, -34) * mm, v(-8.03, -34.4) * mm, v(-7.7, -34.6) * mm, v(-7.43, -34.6) * mm]});
            skFitSpline(sketch, "E612", {"points": [v(-7.43, -34.6) * mm, v(-7.11, -34.6) * mm, v(-6.95, -34.26) * mm, v(-6.95, -33.58) * mm]});
            skFitSpline(sketch, "E613", {"points": [v(-6.95, -33.58) * mm, v(-6.95, -33.1) * mm, v(-7.02, -32.5) * mm, v(-7.15, -31.8) * mm]});
            skFitSpline(sketch, "E614", {"points": [v(-7.15, -31.8) * mm, v(-7.29, -31.1) * mm, v(-7.44, -30.58) * mm, v(-7.62, -30.24) * mm]});
            skFitSpline(sketch, "E615", {"points": [v(-7.62, -30.24) * mm, v(-7.8, -29.9) * mm, v(-7.98, -29.68) * mm, v(-8.18, -29.57) * mm]});
            skFitSpline(sketch, "E616", {"points": [v(-8.18, -29.57) * mm, v(-8.38, -29.46) * mm, v(-8.61, -29.4) * mm, v(-8.87, -29.4) * mm]});
            skFitSpline(sketch, "E617", {"points": [v(-11.29, -29.14) * mm, v(-11.29, -28.69) * mm, v(-11.15, -28.46) * mm, v(-10.86, -28.46) * mm]});
            skFitSpline(sketch, "E618", {"points": [v(-10.86, -28.46) * mm, v(-10.7, -28.46) * mm, v(-10.52, -28.55) * mm, v(-10.3, -28.73) * mm]});
            skFitSpline(sketch, "E619", {"points": [v(-10.3, -28.73) * mm, v(-10.11, -28.93) * mm, v(-9.95, -29.18) * mm, v(-9.83, -29.48) * mm]});
            skFitSpline(sketch, "E620", {"points": [v(-9.83, -29.48) * mm, v(-9.7, -29.78) * mm, v(-9.62, -30.05) * mm, v(-9.57, -30.28) * mm]});
            skFitSpline(sketch, "E621", {"points": [v(-9.57, -30.28) * mm, v(-9.52, -30.5) * mm, v(-9.48, -30.78) * mm, v(-9.46, -31.1) * mm]});
            skFitSpline(sketch, "E622", {"points": [v(-8.99, -35.3) * mm, v(-8.99, -35.79) * mm, v(-9.1, -36.03) * mm, v(-9.32, -36.03) * mm]});
            skFitSpline(sketch, "E623", {"points": [v(-9.32, -36.03) * mm, v(-9.52, -36.03) * mm, v(-9.8, -35.88) * mm, v(-10.17, -35.6) * mm]});
            skFitSpline(sketch, "E624", {"points": [v(-10.17, -35.6) * mm, v(-10.53, -35.35) * mm, v(-11.12, -34.87) * mm, v(-11.93, -34.14) * mm]});
            skFitSpline(sketch, "E625", {"points": [v(-11.93, -34.14) * mm, v(-11.99, -34.08) * mm, v(-12.02, -34.03) * mm, v(-12.05, -33.99) * mm]});
            skFitSpline(sketch, "E626", {"points": [v(-12.05, -33.99) * mm, v(-12.08, -33.95) * mm, v(-12.1, -33.91) * mm, v(-12.1, -33.87) * mm]});
            skFitSpline(sketch, "E627", {"points": [v(-12.1, -33.87) * mm, v(-12.1, -33.85) * mm, v(-12.08, -33.81) * mm, v(-12.01, -33.78) * mm]});
            skFitSpline(sketch, "E628", {"points": [v(-12.01, -33.78) * mm, v(-11.92, -33.78) * mm, v(-11.8, -33.82) * mm, v(-11.67, -33.91) * mm]});
            skFitSpline(sketch, "E629", {"points": [v(-11.67, -33.91) * mm, v(-11.54, -34) * mm, v(-11.41, -34.1) * mm, v(-11.3, -34.18) * mm]});
            skFitSpline(sketch, "E630", {"points": [v(-11.3, -34.18) * mm, v(-11.18, -34.27) * mm, v(-11.07, -34.36) * mm, v(-10.98, -34.45) * mm]});
            skFitSpline(sketch, "E631", {"points": [v(-10.58, -34.75) * mm, v(-10.56, -34.73) * mm, v(-10.55, -34.71) * mm, v(-10.53, -34.68) * mm]});
            skFitSpline(sketch, "E632", {"points": [v(-10.53, -34.68) * mm, v(-10.5, -34.65) * mm, v(-10.5, -34.6) * mm, v(-10.5, -34.51) * mm]});
            skFitSpline(sketch, "E633", {"points": [v(-15.04, -33.96) * mm, v(-14.75, -34.25) * mm, v(-14.54, -34.4) * mm, v(-14.4, -34.4) * mm]});
            skFitSpline(sketch, "E634", {"points": [v(-14.4, -34.4) * mm, v(-14.24, -34.4) * mm, v(-14.16, -34.18) * mm, v(-14.16, -33.74) * mm]});
            skFitSpline(sketch, "E635", {"points": [v(-15.08, -27.43) * mm, v(-15.46, -25.24) * mm, v(-15.66, -23.89) * mm, v(-15.66, -23.38) * mm]});
            skFitSpline(sketch, "E636", {"points": [v(-15.66, -23.38) * mm, v(-15.66, -22.98) * mm, v(-15.57, -22.78) * mm, v(-15.39, -22.78) * mm]});
            skFitSpline(sketch, "E637", {"points": [v(-15.39, -22.78) * mm, v(-15.26, -22.78) * mm, v(-15.13, -22.83) * mm, v(-15, -22.92) * mm]});
            skFitSpline(sketch, "E638", {"points": [v(-14.03, -23.56) * mm, v(-13.56, -23.88) * mm, v(-13.19, -24.12) * mm, v(-12.9, -24.28) * mm]});
            skFitSpline(sketch, "E639", {"points": [v(-12.9, -24.28) * mm, v(-12.62, -24.44) * mm, v(-12.48, -24.6) * mm, v(-12.48, -24.72) * mm]});
            skFitSpline(sketch, "E640", {"points": [v(-12.48, -24.72) * mm, v(-12.5, -24.82) * mm, v(-12.55, -24.87) * mm, v(-12.63, -24.87) * mm]});
            skFitSpline(sketch, "E641", {"points": [v(-12.86, -24.8) * mm, v(-13.36, -24.5) * mm, v(-13.64, -24.35) * mm, v(-13.72, -24.35) * mm]});
            skFitSpline(sketch, "E642", {"points": [v(-13.72, -24.35) * mm, v(-13.85, -24.35) * mm, v(-13.91, -24.49) * mm, v(-13.91, -24.76) * mm]});
            skFitSpline(sketch, "E643", {"points": [v(-12.55, -35.39) * mm, v(-12.55, -35.9) * mm, v(-12.67, -36.16) * mm, v(-12.9, -36.16) * mm]});
            skFitSpline(sketch, "E644", {"points": [v(-12.9, -36.16) * mm, v(-13.25, -36.16) * mm, v(-13.82, -35.77) * mm, v(-14.6, -35) * mm]});
            skFitSpline(sketch, "E645", {"points": [v(-14.6, -35) * mm, v(-15.37, -34.22) * mm, v(-15.75, -33.78) * mm, v(-15.75, -33.66) * mm]});
            skFitSpline(sketch, "E646", {"points": [v(-15.75, -33.66) * mm, v(-15.75, -33.57) * mm, v(-15.7, -33.52) * mm, v(-15.6, -33.52) * mm]});
            skFitSpline(sketch, "E647", {"points": [v(-15.6, -33.52) * mm, v(-15.5, -33.52) * mm, v(-15.32, -33.67) * mm, v(-15.04, -33.96) * mm]});
            skFitSpline(sketch, "E648", {"points": [v(-18.37, -28.75) * mm, v(-17.76, -28.96) * mm, v(-17.33, -29.2) * mm, v(-17.05, -29.48) * mm]});
            skFitSpline(sketch, "E649", {"points": [v(-17.05, -29.48) * mm, v(-16.78, -29.75) * mm, v(-16.52, -30.34) * mm, v(-16.26, -31.23) * mm]});
            skFitSpline(sketch, "E650", {"points": [v(-16.26, -31.23) * mm, v(-16, -32.12) * mm, v(-15.87, -32.85) * mm, v(-15.87, -33.43) * mm]});
            skFitSpline(sketch, "E651", {"points": [v(-15.87, -33.43) * mm, v(-15.87, -34.16) * mm, v(-16.02, -34.78) * mm, v(-16.32, -35.3) * mm]});
            skFitSpline(sketch, "E652", {"points": [v(-16.32, -35.3) * mm, v(-16.61, -35.8) * mm, v(-17.03, -36.06) * mm, v(-17.56, -36.06) * mm]});
            skFitSpline(sketch, "E653", {"points": [v(-17.56, -36.06) * mm, v(-18.1, -36.06) * mm, v(-18.62, -35.9) * mm, v(-19.13, -35.54) * mm]});
            skFitSpline(sketch, "E654", {"points": [v(-20.12, -34.9) * mm, v(-20.3, -34.79) * mm, v(-20.45, -34.68) * mm, v(-20.58, -34.57) * mm]});
            skFitSpline(sketch, "E655", {"points": [v(-20.58, -34.57) * mm, v(-20.71, -34.46) * mm, v(-20.84, -34.34) * mm, v(-20.97, -34.2) * mm]});
            skFitSpline(sketch, "E656", {"points": [v(-20.97, -34.2) * mm, v(-21.1, -34.08) * mm, v(-21.2, -33.86) * mm, v(-21.26, -33.55) * mm]});
            skFitSpline(sketch, "E657", {"points": [v(-21.79, -30.84) * mm, v(-21.79, -30.26) * mm, v(-21.54, -29.7) * mm, v(-21.06, -29.17) * mm]});
            skFitSpline(sketch, "E658", {"points": [v(-21.06, -29.17) * mm, v(-20.57, -28.63) * mm, v(-20.16, -28.37) * mm, v(-19.8, -28.37) * mm]});
            skFitSpline(sketch, "E659", {"points": [v(-18, -30.05) * mm, v(-18.1, -29.8) * mm, v(-18.2, -29.6) * mm, v(-18.3, -29.45) * mm]});
            skFitSpline(sketch, "E660", {"points": [v(-18.3, -29.45) * mm, v(-18.42, -29.32) * mm, v(-18.52, -29.24) * mm, v(-18.58, -29.2) * mm]});
            skFitSpline(sketch, "E661", {"points": [v(-18.58, -29.2) * mm, v(-18.63, -29.16) * mm, v(-18.7, -29.11) * mm, v(-18.79, -29.05) * mm]});
            skFitSpline(sketch, "E662", {"points": [v(-18.79, -29.05) * mm, v(-18.87, -29) * mm, v(-18.97, -28.97) * mm, v(-19.1, -28.97) * mm]});
            skFitSpline(sketch, "E663", {"points": [v(-19.1, -28.97) * mm, v(-19.3, -28.97) * mm, v(-19.5, -29.07) * mm, v(-19.68, -29.29) * mm]});
            skFitSpline(sketch, "E664", {"points": [v(-19.68, -29.29) * mm, v(-19.86, -29.5) * mm, v(-19.96, -29.73) * mm, v(-20, -29.97) * mm]});
            skFitSpline(sketch, "E665", {"points": [v(-20, -29.97) * mm, v(-20.1, -30.43) * mm, v(-20.16, -30.87) * mm, v(-20.16, -31.31) * mm]});
            skFitSpline(sketch, "E666", {"points": [v(-20.16, -31.31) * mm, v(-20.16, -32.05) * mm, v(-20.07, -32.74) * mm, v(-19.9, -33.39) * mm]});
            skFitSpline(sketch, "E667", {"points": [v(-19.9, -33.39) * mm, v(-19.74, -34.03) * mm, v(-19.53, -34.46) * mm, v(-19.3, -34.68) * mm]});
            skFitSpline(sketch, "E668", {"points": [v(-19.3, -34.68) * mm, v(-19.05, -34.9) * mm, v(-18.89, -35) * mm, v(-18.8, -35) * mm]});
            skFitSpline(sketch, "E669", {"points": [v(-18.8, -35) * mm, v(-18.64, -35) * mm, v(-18.45, -34.92) * mm, v(-18.2, -34.77) * mm]});
            skFitSpline(sketch, "E670", {"points": [v(-18.2, -34.77) * mm, v(-17.97, -34.61) * mm, v(-17.78, -34.33) * mm, v(-17.65, -33.91) * mm]});
            skFitSpline(sketch, "E671", {"points": [v(-17.65, -33.91) * mm, v(-17.5, -33.5) * mm, v(-17.44, -33.04) * mm, v(-17.44, -32.53) * mm]});
            skFitSpline(sketch, "E672", {"points": [v(-17.44, -32.53) * mm, v(-17.44, -32.15) * mm, v(-17.47, -31.86) * mm, v(-17.54, -31.66) * mm]});
            skFitSpline(sketch, "E673", {"points": [v(-24.75, -28.75) * mm, v(-24.15, -28.96) * mm, v(-23.7, -29.2) * mm, v(-23.43, -29.48) * mm]});
            skFitSpline(sketch, "E674", {"points": [v(-23.43, -29.48) * mm, v(-23.16, -29.75) * mm, v(-22.9, -30.34) * mm, v(-22.64, -31.23) * mm]});
            skFitSpline(sketch, "E675", {"points": [v(-22.64, -31.23) * mm, v(-22.38, -32.12) * mm, v(-22.25, -32.85) * mm, v(-22.25, -33.43) * mm]});
            skFitSpline(sketch, "E676", {"points": [v(-22.25, -33.43) * mm, v(-22.25, -34.16) * mm, v(-22.4, -34.78) * mm, v(-22.7, -35.3) * mm]});
            skFitSpline(sketch, "E677", {"points": [v(-22.7, -35.3) * mm, v(-23, -35.8) * mm, v(-23.4, -36.06) * mm, v(-23.94, -36.06) * mm]});
            skFitSpline(sketch, "E678", {"points": [v(-23.94, -36.06) * mm, v(-24.48, -36.06) * mm, v(-25, -35.9) * mm, v(-25.5, -35.54) * mm]});
            skFitSpline(sketch, "E679", {"points": [v(-26.5, -34.9) * mm, v(-26.68, -34.79) * mm, v(-26.83, -34.68) * mm, v(-26.96, -34.57) * mm]});
            skFitSpline(sketch, "E680", {"points": [v(-26.96, -34.57) * mm, v(-27.1, -34.46) * mm, v(-27.22, -34.34) * mm, v(-27.35, -34.2) * mm]});
            skFitSpline(sketch, "E681", {"points": [v(-27.35, -34.2) * mm, v(-27.48, -34.08) * mm, v(-27.58, -33.86) * mm, v(-27.64, -33.55) * mm]});
            skFitSpline(sketch, "E682", {"points": [v(-28.17, -30.84) * mm, v(-28.17, -30.26) * mm, v(-27.92, -29.7) * mm, v(-27.44, -29.17) * mm]});
            skFitSpline(sketch, "E683", {"points": [v(-27.44, -29.17) * mm, v(-26.95, -28.63) * mm, v(-26.54, -28.37) * mm, v(-26.19, -28.37) * mm]});
            skFitSpline(sketch, "E684", {"points": [v(-24.38, -30.05) * mm, v(-24.48, -29.8) * mm, v(-24.57, -29.6) * mm, v(-24.68, -29.45) * mm]});
            skFitSpline(sketch, "E685", {"points": [v(-24.68, -29.45) * mm, v(-24.8, -29.32) * mm, v(-24.9, -29.24) * mm, v(-24.96, -29.2) * mm]});
            skFitSpline(sketch, "E686", {"points": [v(-24.96, -29.2) * mm, v(-25.02, -29.16) * mm, v(-25.09, -29.11) * mm, v(-25.17, -29.05) * mm]});
            skFitSpline(sketch, "E687", {"points": [v(-25.17, -29.05) * mm, v(-25.25, -29) * mm, v(-25.35, -28.97) * mm, v(-25.47, -28.97) * mm]});
            skFitSpline(sketch, "E688", {"points": [v(-25.47, -28.97) * mm, v(-25.7, -28.97) * mm, v(-25.89, -29.07) * mm, v(-26.06, -29.29) * mm]});
            skFitSpline(sketch, "E689", {"points": [v(-26.06, -29.29) * mm, v(-26.24, -29.5) * mm, v(-26.34, -29.73) * mm, v(-26.38, -29.97) * mm]});
            skFitSpline(sketch, "E690", {"points": [v(-26.38, -29.97) * mm, v(-26.49, -30.43) * mm, v(-26.54, -30.87) * mm, v(-26.54, -31.31) * mm]});
            skFitSpline(sketch, "E691", {"points": [v(-26.54, -31.31) * mm, v(-26.54, -32.05) * mm, v(-26.45, -32.74) * mm, v(-26.29, -33.39) * mm]});
            skFitSpline(sketch, "E692", {"points": [v(-26.29, -33.39) * mm, v(-26.12, -34.03) * mm, v(-25.91, -34.46) * mm, v(-25.67, -34.68) * mm]});
            skFitSpline(sketch, "E693", {"points": [v(-25.67, -34.68) * mm, v(-25.43, -34.9) * mm, v(-25.27, -35) * mm, v(-25.18, -35) * mm]});
            skFitSpline(sketch, "E694", {"points": [v(-25.18, -35) * mm, v(-25.02, -35) * mm, v(-24.83, -34.92) * mm, v(-24.59, -34.77) * mm]});
            skFitSpline(sketch, "E695", {"points": [v(-24.59, -34.77) * mm, v(-24.35, -34.61) * mm, v(-24.16, -34.33) * mm, v(-24.03, -33.91) * mm]});
            skFitSpline(sketch, "E696", {"points": [v(-24.03, -33.91) * mm, v(-23.9, -33.5) * mm, v(-23.82, -33.04) * mm, v(-23.82, -32.53) * mm]});
            skFitSpline(sketch, "E697", {"points": [v(-23.82, -32.53) * mm, v(-23.82, -32.15) * mm, v(-23.85, -31.86) * mm, v(-23.92, -31.66) * mm]});
            skFitSpline(sketch, "E698", {"points": [v(-29.49, -30.2) * mm, v(-29.52, -29.94) * mm, v(-29.64, -29.77) * mm, v(-29.82, -29.71) * mm]});
            skFitSpline(sketch, "E699", {"points": [v(-29.82, -29.71) * mm, v(-30.01, -29.65) * mm, v(-30.34, -29.63) * mm, v(-30.82, -29.63) * mm]});
            skFitSpline(sketch, "E700", {"points": [v(-32.6, -29.59) * mm, v(-32.3, -30.26) * mm, v(-31.89, -31) * mm, v(-31.38, -31.82) * mm]});
            skFitSpline(sketch, "E701", {"points": [v(-31.38, -31.82) * mm, v(-30.87, -32.63) * mm, v(-30.37, -33.32) * mm, v(-29.9, -33.87) * mm]});
            skFitSpline(sketch, "E702", {"points": [v(-29.9, -33.87) * mm, v(-29.43, -34.43) * mm, v(-28.81, -35.04) * mm, v(-28.05, -35.7) * mm]});
            skFitSpline(sketch, "E703", {"points": [v(-28.34, -36) * mm, v(-28.77, -35.68) * mm, v(-29.35, -35.2) * mm, v(-30.1, -34.53) * mm]});
            skFitSpline(sketch, "E704", {"points": [v(-30.1, -34.53) * mm, v(-30.84, -33.87) * mm, v(-31.53, -33.1) * mm, v(-32.16, -32.19) * mm]});
            skFitSpline(sketch, "E705", {"points": [v(-34.28, -28.64) * mm, v(-34.3, -28.6) * mm, v(-34.31, -28.54) * mm, v(-34.31, -28.46) * mm]});
            skFitSpline(sketch, "E706", {"points": [v(-34.31, -28.46) * mm, v(-34.31, -28.37) * mm, v(-34.27, -28.33) * mm, v(-34.18, -28.33) * mm]});
            skFitSpline(sketch, "E707", {"points": [v(-34.02, -28.38) * mm, v(-33.87, -28.5) * mm, v(-33.58, -28.56) * mm, v(-33.17, -28.56) * mm]});
            skFitSpline(sketch, "E708", {"points": [v(-30.4, -28.23) * mm, v(-30.06, -28.23) * mm, v(-29.8, -28.29) * mm, v(-29.6, -28.4) * mm]});
            skFitSpline(sketch, "E709", {"points": [v(-29.6, -28.4) * mm, v(-29.4, -28.52) * mm, v(-29.28, -28.65) * mm, v(-29.22, -28.8) * mm]});
            skFitSpline(sketch, "E710", {"points": [v(-29.22, -28.8) * mm, v(-29.17, -28.93) * mm, v(-29.12, -29.12) * mm, v(-29.1, -29.33) * mm]});
            skFitSpline(sketch, "E711", {"points": [v(-29.02, -30) * mm, v(-29.02, -30.4) * mm, v(-29.1, -30.61) * mm, v(-29.23, -30.61) * mm]});
            skFitSpline(sketch, "E712", {"points": [v(-29.23, -30.61) * mm, v(-29.36, -30.61) * mm, v(-29.45, -30.48) * mm, v(-29.49, -30.2) * mm]});
            skFitSpline(sketch, "E713", {"points": [v(-28.22, -35.85) * mm, v(-28.25, -35.88) * mm, v(-28.3, -35.9) * mm, v(-28.4, -35.95) * mm]});
            skFitSpline(sketch, "E714", {"points": [v(-29.27, -35.27) * mm, v(-29.45, -35.15) * mm, v(-29.62, -35.1) * mm, v(-29.78, -35.1) * mm]});
            skFitSpline(sketch, "E715", {"points": [v(-29.78, -35.1) * mm, v(-30.02, -35.1) * mm, v(-30.42, -35.3) * mm, v(-30.96, -35.68) * mm]});
            skFitSpline(sketch, "E716", {"points": [v(-30.96, -35.68) * mm, v(-31.27, -35.94) * mm, v(-31.63, -36.06) * mm, v(-32.03, -36.06) * mm]});
            skFitSpline(sketch, "E717", {"points": [v(-32.03, -36.06) * mm, v(-32.43, -36.06) * mm, v(-32.81, -35.93) * mm, v(-33.19, -35.66) * mm]});
            skFitSpline(sketch, "E718", {"points": [v(-33.19, -35.66) * mm, v(-33.56, -35.4) * mm, v(-33.83, -35.1) * mm, v(-33.98, -34.79) * mm]});
            skFitSpline(sketch, "E719", {"points": [v(-33.98, -34.79) * mm, v(-34.14, -34.47) * mm, v(-34.22, -34.25) * mm, v(-34.22, -34.12) * mm]});
            skFitSpline(sketch, "E720", {"points": [v(-34.22, -34.12) * mm, v(-34.22, -34.07) * mm, v(-34.19, -34.02) * mm, v(-34.12, -33.97) * mm]});
            skFitSpline(sketch, "E721", {"points": [v(-34.12, -33.97) * mm, v(-34, -33.97) * mm, v(-33.9, -34.05) * mm, v(-33.83, -34.22) * mm]});
            skFitSpline(sketch, "E722", {"points": [v(-33.83, -34.22) * mm, v(-33.56, -34.62) * mm, v(-33.23, -34.82) * mm, v(-32.84, -34.82) * mm]});
            skFitSpline(sketch, "E723", {"points": [v(-32.84, -34.82) * mm, v(-32.71, -34.82) * mm, v(-32.6, -34.81) * mm, v(-32.48, -34.78) * mm]});
            skFitSpline(sketch, "E724", {"points": [v(-32.48, -34.78) * mm, v(-32.37, -34.76) * mm, v(-32.25, -34.72) * mm, v(-32.12, -34.67) * mm]});
            skFitSpline(sketch, "E725", {"points": [v(-30.22, -33.8) * mm, v(-30.1, -33.74) * mm, v(-29.98, -33.72) * mm, v(-29.83, -33.72) * mm]});
            skFitSpline(sketch, "E726", {"points": [v(-29.83, -33.72) * mm, v(-29.5, -33.72) * mm, v(-29.2, -33.86) * mm, v(-28.91, -34.13) * mm]});
            skFitSpline(sketch, "E727", {"points": [v(-28.91, -34.13) * mm, v(-28.64, -34.41) * mm, v(-28.45, -34.73) * mm, v(-28.36, -35.08) * mm]});
            skFitSpline(sketch, "E728", {"points": [v(-39.76, -29.33) * mm, v(-39.87, -29.28) * mm, v(-39.95, -29.19) * mm, v(-40.03, -29.06) * mm]});
            skFitSpline(sketch, "E729", {"points": [v(-40.03, -29.06) * mm, v(-40.1, -28.94) * mm, v(-40.13, -28.82) * mm, v(-40.13, -28.72) * mm]});
            skFitSpline(sketch, "E730", {"points": [v(-40.13, -28.72) * mm, v(-40.13, -28.52) * mm, v(-39.94, -28.42) * mm, v(-39.55, -28.42) * mm]});
            skFitSpline(sketch, "E731", {"points": [v(-38.08, -28.55) * mm, v(-37.73, -28.55) * mm, v(-37.4, -28.64) * mm, v(-37.09, -28.8) * mm]});
            skFitSpline(sketch, "E732", {"points": [v(-37.09, -28.8) * mm, v(-36.78, -28.96) * mm, v(-36.43, -29.24) * mm, v(-36.06, -29.65) * mm]});
            skFitSpline(sketch, "E733", {"points": [v(-36.06, -29.65) * mm, v(-35.68, -30.06) * mm, v(-35.4, -30.54) * mm, v(-35.19, -31.09) * mm]});
            skFitSpline(sketch, "E734", {"points": [v(-35.19, -31.09) * mm, v(-34.98, -31.63) * mm, v(-34.83, -32.08) * mm, v(-34.74, -32.43) * mm]});
            skFitSpline(sketch, "E735", {"points": [v(-34.74, -32.43) * mm, v(-34.65, -32.78) * mm, v(-34.58, -33.1) * mm, v(-34.54, -33.38) * mm]});
            skFitSpline(sketch, "E736", {"points": [v(-34.54, -33.38) * mm, v(-34.5, -33.67) * mm, v(-34.46, -33.9) * mm, v(-34.45, -34.1) * mm]});
            skFitSpline(sketch, "E737", {"points": [v(-34.45, -34.1) * mm, v(-34.44, -34.28) * mm, v(-34.43, -34.42) * mm, v(-34.43, -34.5) * mm]});
            skFitSpline(sketch, "E738", {"points": [v(-34.43, -34.5) * mm, v(-34.43, -35.53) * mm, v(-34.71, -36.04) * mm, v(-35.28, -36.04) * mm]});
            skFitSpline(sketch, "E739", {"points": [v(-35.28, -36.04) * mm, v(-35.81, -36.04) * mm, v(-36.55, -35.55) * mm, v(-37.5, -34.56) * mm]});
            skFitSpline(sketch, "E740", {"points": [v(-38.15, -33.84) * mm, v(-38.36, -33.63) * mm, v(-38.53, -33.42) * mm, v(-38.66, -33.2) * mm]});
            skFitSpline(sketch, "E741", {"points": [v(-38.66, -33.2) * mm, v(-38.79, -32.97) * mm, v(-38.85, -32.75) * mm, v(-38.85, -32.53) * mm]});
            skFitSpline(sketch, "E742", {"points": [v(-38.85, -32.53) * mm, v(-38.85, -32.47) * mm, v(-38.83, -32.39) * mm, v(-38.77, -32.3) * mm]});
            skFitSpline(sketch, "E743", {"points": [v(-38.33, -32.84) * mm, v(-38.06, -33.22) * mm, v(-37.73, -33.61) * mm, v(-37.36, -34) * mm]});
            skFitSpline(sketch, "E744", {"points": [v(-37.36, -34) * mm, v(-36.98, -34.4) * mm, v(-36.66, -34.6) * mm, v(-36.39, -34.6) * mm]});
            skFitSpline(sketch, "E745", {"points": [v(-36.39, -34.6) * mm, v(-36.07, -34.6) * mm, v(-35.9, -34.26) * mm, v(-35.9, -33.58) * mm]});
            skFitSpline(sketch, "E746", {"points": [v(-35.9, -33.58) * mm, v(-35.9, -33.1) * mm, v(-35.97, -32.5) * mm, v(-36.1, -31.8) * mm]});
            skFitSpline(sketch, "E747", {"points": [v(-36.1, -31.8) * mm, v(-36.24, -31.1) * mm, v(-36.4, -30.58) * mm, v(-36.57, -30.24) * mm]});
            skFitSpline(sketch, "E748", {"points": [v(-36.57, -30.24) * mm, v(-36.75, -29.9) * mm, v(-36.94, -29.68) * mm, v(-37.14, -29.57) * mm]});
            skFitSpline(sketch, "E749", {"points": [v(-37.14, -29.57) * mm, v(-37.34, -29.46) * mm, v(-37.57, -29.4) * mm, v(-37.82, -29.4) * mm]});
            skFitSpline(sketch, "E750", {"points": [v(-40.24, -29.14) * mm, v(-40.24, -28.69) * mm, v(-40.1, -28.46) * mm, v(-39.82, -28.46) * mm]});
            skFitSpline(sketch, "E751", {"points": [v(-39.82, -28.46) * mm, v(-39.66, -28.46) * mm, v(-39.48, -28.55) * mm, v(-39.26, -28.73) * mm]});
            skFitSpline(sketch, "E752", {"points": [v(-39.26, -28.73) * mm, v(-39.07, -28.93) * mm, v(-38.9, -29.18) * mm, v(-38.79, -29.48) * mm]});
            skFitSpline(sketch, "E753", {"points": [v(-38.79, -29.48) * mm, v(-38.66, -29.78) * mm, v(-38.58, -30.05) * mm, v(-38.53, -30.28) * mm]});
            skFitSpline(sketch, "E754", {"points": [v(-38.53, -30.28) * mm, v(-38.47, -30.5) * mm, v(-38.44, -30.78) * mm, v(-38.41, -31.1) * mm]});
            skFitSpline(sketch, "E755", {"points": [v(-37.94, -35.3) * mm, v(-37.94, -35.79) * mm, v(-38.05, -36.03) * mm, v(-38.27, -36.03) * mm]});
            skFitSpline(sketch, "E756", {"points": [v(-38.27, -36.03) * mm, v(-38.48, -36.03) * mm, v(-38.76, -35.88) * mm, v(-39.12, -35.6) * mm]});
            skFitSpline(sketch, "E757", {"points": [v(-39.12, -35.6) * mm, v(-39.49, -35.35) * mm, v(-40.07, -34.87) * mm, v(-40.89, -34.14) * mm]});
            skFitSpline(sketch, "E758", {"points": [v(-40.89, -34.14) * mm, v(-40.94, -34.08) * mm, v(-40.98, -34.03) * mm, v(-41, -33.99) * mm]});
            skFitSpline(sketch, "E759", {"points": [v(-41, -33.99) * mm, v(-41.03, -33.95) * mm, v(-41.05, -33.91) * mm, v(-41.06, -33.87) * mm]});
            skFitSpline(sketch, "E760", {"points": [v(-41.06, -33.87) * mm, v(-41.06, -33.85) * mm, v(-41.03, -33.81) * mm, v(-40.97, -33.78) * mm]});
            skFitSpline(sketch, "E761", {"points": [v(-40.97, -33.78) * mm, v(-40.88, -33.78) * mm, v(-40.76, -33.82) * mm, v(-40.63, -33.91) * mm]});
            skFitSpline(sketch, "E762", {"points": [v(-40.63, -33.91) * mm, v(-40.5, -34) * mm, v(-40.37, -34.1) * mm, v(-40.25, -34.18) * mm]});
            skFitSpline(sketch, "E763", {"points": [v(-40.25, -34.18) * mm, v(-40.13, -34.27) * mm, v(-40.03, -34.36) * mm, v(-39.94, -34.45) * mm]});
            skFitSpline(sketch, "E764", {"points": [v(-39.53, -34.75) * mm, v(-39.52, -34.73) * mm, v(-39.5, -34.71) * mm, v(-39.48, -34.68) * mm]});
            skFitSpline(sketch, "E765", {"points": [v(-39.48, -34.68) * mm, v(-39.46, -34.65) * mm, v(-39.45, -34.6) * mm, v(-39.45, -34.51) * mm]});
            skFitSpline(sketch, "E766", {"points": [v(22.3, -54) * mm, v(22.86, -53.32) * mm, v(23.74, -52.78) * mm, v(24.93, -52.38) * mm]});
            skFitSpline(sketch, "E767", {"points": [v(24.93, -52.38) * mm, v(25.54, -52.18) * mm, v(26.1, -52.02) * mm, v(26.63, -51.9) * mm]});
            skFitSpline(sketch, "E768", {"points": [v(26.63, -51.9) * mm, v(27.16, -51.8) * mm, v(27.71, -51.68) * mm, v(28.28, -51.56) * mm]});
            skFitSpline(sketch, "E769", {"points": [v(28.28, -51.56) * mm, v(29.15, -51.37) * mm, v(29.75, -51.17) * mm, v(30.06, -50.94) * mm]});
            skFitSpline(sketch, "E770", {"points": [v(30.06, -50.94) * mm, v(30.37, -50.72) * mm, v(30.53, -50.4) * mm, v(30.53, -49.98) * mm]});
            skFitSpline(sketch, "E771", {"points": [v(30.53, -49.98) * mm, v(30.53, -49.7) * mm, v(30.43, -49.45) * mm, v(30.24, -49.23) * mm]});
            skFitSpline(sketch, "E772", {"points": [v(30.24, -49.23) * mm, v(30.04, -49.02) * mm, v(29.8, -48.86) * mm, v(29.54, -48.75) * mm]});
            skFitSpline(sketch, "E773", {"points": [v(29.54, -48.75) * mm, v(29.23, -48.62) * mm, v(28.91, -48.53) * mm, v(28.58, -48.49) * mm]});
            skFitSpline(sketch, "E774", {"points": [v(28.58, -48.49) * mm, v(28.25, -48.44) * mm, v(27.92, -48.42) * mm, v(27.58, -48.42) * mm]});
            skFitSpline(sketch, "E775", {"points": [v(27.58, -48.42) * mm, v(26.63, -48.42) * mm, v(25.7, -48.6) * mm, v(24.8, -48.94) * mm]});
            skFitSpline(sketch, "E776", {"points": [v(24.8, -48.94) * mm, v(23.88, -49.28) * mm, v(23.11, -49.7) * mm, v(22.49, -50.22) * mm]});
            skFitSpline(sketch, "E777", {"points": [v(22.06, -46.56) * mm, v(22.8, -46.25) * mm, v(23.66, -46) * mm, v(24.66, -45.8) * mm]});
            skFitSpline(sketch, "E778", {"points": [v(24.66, -45.8) * mm, v(25.66, -45.6) * mm, v(26.67, -45.5) * mm, v(27.7, -45.5) * mm]});
            skFitSpline(sketch, "E779", {"points": [v(27.7, -45.5) * mm, v(29.74, -45.5) * mm, v(31.41, -45.96) * mm, v(32.71, -46.9) * mm]});
            skFitSpline(sketch, "E780", {"points": [v(32.71, -46.9) * mm, v(34.01, -47.83) * mm, v(34.66, -49.04) * mm, v(34.66, -50.52) * mm]});
            skFitSpline(sketch, "E781", {"points": [v(34.66, -50.52) * mm, v(34.66, -51.62) * mm, v(34.38, -52.55) * mm, v(33.8, -53.29) * mm]});
            skFitSpline(sketch, "E782", {"points": [v(33.8, -53.29) * mm, v(33.23, -54.03) * mm, v(32.28, -54.62) * mm, v(30.97, -55.06) * mm]});
            skFitSpline(sketch, "E783", {"points": [v(30.97, -55.06) * mm, v(30.4, -55.25) * mm, v(29.79, -55.4) * mm, v(29.13, -55.53) * mm]});
            skFitSpline(sketch, "E784", {"points": [v(29.13, -55.53) * mm, v(28.48, -55.66) * mm, v(27.86, -55.79) * mm, v(27.28, -55.93) * mm]});
            skFitSpline(sketch, "E785", {"points": [v(27.28, -55.93) * mm, v(26.72, -56.07) * mm, v(26.3, -56.26) * mm, v(26, -56.51) * mm]});
            skFitSpline(sketch, "E786", {"points": [v(26, -56.51) * mm, v(25.72, -56.77) * mm, v(25.57, -57.07) * mm, v(25.57, -57.42) * mm]});
            skFitSpline(sketch, "E787", {"points": [v(25.57, -57.42) * mm, v(25.57, -57.8) * mm, v(25.67, -58.08) * mm, v(25.87, -58.27) * mm]});
            skFitSpline(sketch, "E788", {"points": [v(25.87, -58.27) * mm, v(26.07, -58.46) * mm, v(26.32, -58.62) * mm, v(26.63, -58.75) * mm]});
            skFitSpline(sketch, "E789", {"points": [v(26.63, -58.75) * mm, v(26.88, -58.85) * mm, v(27.2, -58.92) * mm, v(27.6, -58.96) * mm]});
            skFitSpline(sketch, "E790", {"points": [v(27.6, -58.96) * mm, v(28, -59) * mm, v(28.32, -59.03) * mm, v(28.56, -59.03) * mm]});
            skFitSpline(sketch, "E791", {"points": [v(28.56, -59.03) * mm, v(29.51, -59.03) * mm, v(30.5, -58.85) * mm, v(31.53, -58.48) * mm]});
            skFitSpline(sketch, "E792", {"points": [v(31.53, -58.48) * mm, v(32.56, -58.12) * mm, v(33.49, -57.6) * mm, v(34.32, -56.92) * mm]});
            skFitSpline(sketch, "E793", {"points": [v(34.76, -60.73) * mm, v(33.92, -61.1) * mm, v(33.02, -61.38) * mm, v(32.06, -61.62) * mm]});
            skFitSpline(sketch, "E794", {"points": [v(32.06, -61.62) * mm, v(31.1, -61.85) * mm, v(29.98, -61.96) * mm, v(28.7, -61.96) * mm]});
            skFitSpline(sketch, "E795", {"points": [v(28.7, -61.96) * mm, v(26.46, -61.96) * mm, v(24.7, -61.47) * mm, v(23.4, -60.5) * mm]});
            skFitSpline(sketch, "E796", {"points": [v(23.4, -60.5) * mm, v(22.1, -59.52) * mm, v(21.44, -58.24) * mm, v(21.44, -56.68) * mm]});
            skFitSpline(sketch, "E797", {"points": [v(21.44, -56.68) * mm, v(21.44, -55.58) * mm, v(21.72, -54.7) * mm, v(22.3, -54) * mm]});
            skSolve(sketch);
        }
        {
            var Q0;
            Q0=qSketchRegion(id+"F0",true);
            extrude(context, id + "F2", {"entities" : qUnion([Q0]), "depth" : 0.8 * mm, "offsetDistance" : 25 * mm, "symmetric" : true});
        }
        {
            var Q0;
            Q0=qSketchRegion(id+"F1",true);
            var Q1;
            Q1=makeQuery(id+"F2.opExtrude","CAP_FACE",FACE,{"disambiguationData":[OSD([sQuery(id+"F0.wireOp",EDGE,"E0.bottom"),sQuery(id+"F0.wireOp",EDGE,"E0.top"),sQuery(id+"F0.wireOp",EDGE,"E0.left"),sQuery(id+"F0.wireOp",EDGE,"E0.right"),sQuery(id+"F0.wireOp",EDGE,"E1"),sQuery(id+"F0.wireOp",EDGE,"E2.filletArc"),sQuery(id+"F0.wireOp",EDGE,"E3.filletArc"),sQuery(id+"F0.wireOp",EDGE,"E4.filletArc"),sQuery(id+"F0.wireOp",EDGE,"E5.filletArc")])],"isStart":true});
            extrude(context, id + "F3", {"entities" : qUnion([Q0]), "operationType" : NewBodyOperationType.REMOVE, "endBound" : BoundingType.UP_TO_SURFACE, "oppositeDirection" : true, "depth" : 25 * mm, "endBoundEntityFace" : qUnion([Q1]), "offsetDistance" : 25 * mm});
        }
        {
            var Q0;
            Q0=qSketchRegion(id+"F1",true);
            var Q1;
            {var subQ27=sQuery(id+"F0.wireOp",EDGE,"E4.filletArc");var subQ29=sQuery(id+"F0.wireOp",EDGE,"E0.left");var subQ31=sQuery(id+"F0.wireOp",EDGE,"E0.top");var subQ32=sQuery(id+"F0.wireOp",EDGE,"E0.right");var subQ33=sQuery(id+"F0.wireOp",EDGE,"E1");var subQ34=sQuery(id+"F0.wireOp",EDGE,"E0.bottom");var subQ37=sQuery(id+"F0.wireOp",EDGE,"E2.filletArc");var subQ39=sQuery(id+"F0.wireOp",EDGE,"E5.filletArc");var subQ40=sQuery(id+"F0.wireOp",EDGE,"E3.filletArc");Q1=makeQuery(id+"F3.boolean.opBoolean","SPLIT",FACE,{"disambiguationData":[TD([makeQuery(id+"F2.opExtrude","SWEPT_FACE",FACE,{"disambiguationData":[OSD([subQ34])]})])],"derivedFrom":makeQuery(id+"F2.opExtrude","CAP_FACE",FACE,{"disambiguationData":[OSD([subQ34,subQ31,subQ29,subQ32,subQ33,subQ37,subQ40,subQ27,subQ39])],"isStart":true})});}
            extrude(context, id + "F4", {"entities" : qUnion([Q0]), "endBound" : BoundingType.UP_TO_SURFACE, "oppositeDirection" : true, "depth" : 25 * mm, "endBoundEntityFace" : qUnion([Q1]), "offsetDistance" : 25 * mm});
        }
        {
            var Q0;
            Q0=makeQuery(id+"F2.opExtrude","CAP_FACE",FACE,{"disambiguationData":[OSD([sQuery(id+"F0.wireOp",EDGE,"E0.bottom"),sQuery(id+"F0.wireOp",EDGE,"E0.top"),sQuery(id+"F0.wireOp",EDGE,"E0.left"),sQuery(id+"F0.wireOp",EDGE,"E0.right"),sQuery(id+"F0.wireOp",EDGE,"E1"),sQuery(id+"F0.wireOp",EDGE,"E2.filletArc"),sQuery(id+"F0.wireOp",EDGE,"E3.filletArc"),sQuery(id+"F0.wireOp",EDGE,"E4.filletArc"),sQuery(id+"F0.wireOp",EDGE,"E5.filletArc"),sQuery(id+"F0.wireOp",EDGE,"E6"),sQuery(id+"F0.wireOp",EDGE,"E7.filletArc"),sQuery(id+"F0.wireOp",EDGE,"E8"),sQuery(id+"F0.wireOp",EDGE,"E9.filletArc")])],"isStart":false});
            var sketch = newSketch(context, id + "F5", { "sketchPlane" : qUnion([Q0])});
            skLineSegment(sketch, "E798", {"start": v(-21.56, -50.32) * mm, "end": v(-17.06, -50.32) * mm});
            skLineSegment(sketch, "E799", {"start": v(-17.06, -50.32) * mm, "end": v(-17.06, -46.04) * mm});
            skLineSegment(sketch, "E800", {"start": v(-17.06, -46.04) * mm, "end": v(-19.49, -46.04) * mm});
            skLineSegment(sketch, "E801", {"start": v(-19.49, -46.04) * mm, "end": v(-23.43, -46.04) * mm});
            skLineSegment(sketch, "E802", {"start": v(-23.43, -46.04) * mm, "end": v(-21.56, -50.32) * mm});
            skLineSegment(sketch, "E803", {"start": v(-23.43, -60.42) * mm, "end": v(-17.06, -60.42) * mm});
            skLineSegment(sketch, "E804", {"start": v(-17.06, -60.42) * mm, "end": v(-17.06, -56.14) * mm});
            skLineSegment(sketch, "E805", {"start": v(-17.06, -56.14) * mm, "end": v(-21.56, -56.14) * mm});
            skLineSegment(sketch, "E806", {"start": v(-21.56, -56.14) * mm, "end": v(-23.43, -60.42) * mm});
            skLineSegment(sketch, "E807", {"start": v(-1.16, -46.04) * mm, "end": v(3.9, -60.42) * mm});
            skLineSegment(sketch, "E808", {"start": v(3.9, -60.42) * mm, "end": v(11.52, -60.42) * mm});
            skLineSegment(sketch, "E809", {"start": v(11.52, -60.42) * mm, "end": v(16.65, -46.04) * mm});
            skLineSegment(sketch, "E810", {"start": v(16.65, -46.04) * mm, "end": v(10.89, -46.04) * mm});
            skLineSegment(sketch, "E811", {"start": v(10.89, -46.04) * mm, "end": v(7.58, -57.08) * mm});
            skLineSegment(sketch, "E812", {"start": v(7.58, -57.08) * mm, "end": v(4.32, -46.04) * mm});
            skLineSegment(sketch, "E813", {"start": v(4.32, -46.04) * mm, "end": v(-1.16, -46.04) * mm});
            skLineSegment(sketch, "E814", {"start": v(20.21, -60.42) * mm, "end": v(21.12, -57.83) * mm});
            skLineSegment(sketch, "E815", {"start": v(21.12, -57.83) * mm, "end": v(25.39, -57.83) * mm});
            skLineSegment(sketch, "E816", {"start": v(25.39, -57.83) * mm, "end": v(26.3, -60.42) * mm});
            skLineSegment(sketch, "E817", {"start": v(26.3, -60.42) * mm, "end": v(31.73, -60.42) * mm});
            skLineSegment(sketch, "E818", {"start": v(31.73, -60.42) * mm, "end": v(26.92, -46.04) * mm});
            skLineSegment(sketch, "E819", {"start": v(26.92, -46.04) * mm, "end": v(19.79, -46.04) * mm});
            skLineSegment(sketch, "E820", {"start": v(19.79, -46.04) * mm, "end": v(15.06, -60.42) * mm});
            skLineSegment(sketch, "E821", {"start": v(15.06, -60.42) * mm, "end": v(20.21, -60.42) * mm});
            skLineSegment(sketch, "E822", {"start": v(25.27, -54.92) * mm, "end": v(21.3, -54.92) * mm});
            skLineSegment(sketch, "E823", {"start": v(21.3, -54.92) * mm, "end": v(23.37, -49.23) * mm});
            skLineSegment(sketch, "E824", {"start": v(23.37, -49.23) * mm, "end": v(25.27, -54.92) * mm});
            skFitSpline(sketch, "E825", {"points": [v(-23.63, -56.07) * mm, v(-24.1, -56.02) * mm, v(-24.54, -55.94) * mm, v(-24.98, -55.82) * mm]});
            skFitSpline(sketch, "E826", {"points": [v(-24.98, -55.82) * mm, v(-25.42, -55.7) * mm, v(-25.79, -55.46) * mm, v(-26.1, -55.1) * mm]});
            skFitSpline(sketch, "E827", {"points": [v(-26.1, -55.1) * mm, v(-26.4, -54.73) * mm, v(-26.57, -54.12) * mm, v(-26.6, -53.27) * mm]});
            skFitSpline(sketch, "E828", {"points": [v(-26.6, -53.27) * mm, v(-26.56, -52.4) * mm, v(-26.39, -51.78) * mm, v(-26.1, -51.44) * mm]});
            skFitSpline(sketch, "E829", {"points": [v(-26.1, -51.44) * mm, v(-25.8, -51.1) * mm, v(-25.47, -50.85) * mm, v(-25.09, -50.71) * mm]});
            skFitSpline(sketch, "E830", {"points": [v(-25.09, -50.71) * mm, v(-24.71, -50.57) * mm, v(-24.28, -50.47) * mm, v(-23.8, -50.41) * mm]});
            skFitSpline(sketch, "E831", {"points": [v(-23.8, -50.41) * mm, v(-23.31, -50.35) * mm, v(-22.57, -50.32) * mm, v(-21.56, -50.32) * mm]});
            skFitSpline(sketch, "E832", {"points": [v(-23.43, -46.04) * mm, v(-24.56, -46.04) * mm, v(-25.62, -46.19) * mm, v(-26.62, -46.48) * mm]});
            skFitSpline(sketch, "E833", {"points": [v(-26.62, -46.48) * mm, v(-27.62, -46.77) * mm, v(-28.5, -47.2) * mm, v(-29.27, -47.8) * mm]});
            skFitSpline(sketch, "E834", {"points": [v(-29.27, -47.8) * mm, v(-30.04, -48.38) * mm, v(-30.64, -49.12) * mm, v(-31.08, -50) * mm]});
            skFitSpline(sketch, "E835", {"points": [v(-31.08, -50) * mm, v(-31.51, -50.89) * mm, v(-31.73, -51.9) * mm, v(-31.73, -53.02) * mm]});
            skFitSpline(sketch, "E836", {"points": [v(-31.73, -53.02) * mm, v(-31.73, -54.63) * mm, v(-31.36, -55.98) * mm, v(-30.64, -57.1) * mm]});
            skFitSpline(sketch, "E837", {"points": [v(-30.64, -57.1) * mm, v(-29.91, -58.2) * mm, v(-28.92, -59.03) * mm, v(-27.66, -59.59) * mm]});
            skFitSpline(sketch, "E838", {"points": [v(-27.66, -59.59) * mm, v(-26.4, -60.14) * mm, v(-24.99, -60.42) * mm, v(-23.43, -60.42) * mm]});
            skFitSpline(sketch, "E839", {"points": [v(-21.56, -56.14) * mm, v(-22.47, -56.14) * mm, v(-23.16, -56.11) * mm, v(-23.63, -56.07) * mm]});
            skFitSpline(sketch, "E840", {"points": [v(-1.44, -49.3) * mm, v(-2.1, -48.19) * mm, v(-3.05, -47.35) * mm, v(-4.3, -46.79) * mm]});
            skFitSpline(sketch, "E841", {"points": [v(-4.3, -46.79) * mm, v(-5.55, -46.22) * mm, v(-7.03, -45.94) * mm, v(-8.75, -45.94) * mm]});
            skFitSpline(sketch, "E842", {"points": [v(-8.75, -45.94) * mm, v(-10.04, -45.94) * mm, v(-11.2, -46.1) * mm, v(-12.22, -46.42) * mm]});
            skFitSpline(sketch, "E843", {"points": [v(-12.22, -46.42) * mm, v(-13.24, -46.74) * mm, v(-14.1, -47.21) * mm, v(-14.8, -47.84) * mm]});
            skFitSpline(sketch, "E844", {"points": [v(-14.8, -47.84) * mm, v(-15.51, -48.46) * mm, v(-16.05, -49.23) * mm, v(-16.41, -50.14) * mm]});
            skFitSpline(sketch, "E845", {"points": [v(-16.41, -50.14) * mm, v(-16.78, -51.05) * mm, v(-16.96, -52.1) * mm, v(-16.96, -53.31) * mm]});
            skFitSpline(sketch, "E846", {"points": [v(-16.96, -53.31) * mm, v(-16.96, -54.9) * mm, v(-16.64, -56.24) * mm, v(-16, -57.34) * mm]});
            skFitSpline(sketch, "E847", {"points": [v(-16, -57.34) * mm, v(-15.37, -58.43) * mm, v(-14.43, -59.26) * mm, v(-13.2, -59.82) * mm]});
            skFitSpline(sketch, "E848", {"points": [v(-13.2, -59.82) * mm, v(-11.95, -60.38) * mm, v(-10.47, -60.66) * mm, v(-8.75, -60.66) * mm]});
            skFitSpline(sketch, "E849", {"points": [v(-8.75, -60.66) * mm, v(-7.02, -60.66) * mm, v(-5.54, -60.39) * mm, v(-4.3, -59.83) * mm]});
            skFitSpline(sketch, "E850", {"points": [v(-4.3, -59.83) * mm, v(-3.05, -59.27) * mm, v(-2.1, -58.44) * mm, v(-1.44, -57.33) * mm]});
            skFitSpline(sketch, "E851", {"points": [v(-1.44, -57.33) * mm, v(-0.79, -56.22) * mm, v(-0.46, -54.88) * mm, v(-0.46, -53.31) * mm]});
            skFitSpline(sketch, "E852", {"points": [v(-0.46, -53.31) * mm, v(-0.46, -51.74) * mm, v(-0.79, -50.4) * mm, v(-1.44, -49.3) * mm]});
            skFitSpline(sketch, "E853", {"points": [v(-8.78, -49.9) * mm, v(-7.48, -49.9) * mm, v(-6.62, -50.25) * mm, v(-6.22, -50.94) * mm]});
            skFitSpline(sketch, "E854", {"points": [v(-6.22, -50.94) * mm, v(-5.82, -51.62) * mm, v(-5.6, -52.43) * mm, v(-5.55, -53.35) * mm]});
            skFitSpline(sketch, "E855", {"points": [v(-5.55, -53.35) * mm, v(-5.6, -54) * mm, v(-5.67, -54.56) * mm, v(-5.79, -55.02) * mm]});
            skFitSpline(sketch, "E856", {"points": [v(-5.79, -55.02) * mm, v(-5.9, -55.48) * mm, v(-6.2, -55.89) * mm, v(-6.66, -56.25) * mm]});
            skFitSpline(sketch, "E857", {"points": [v(-6.66, -56.25) * mm, v(-7.13, -56.6) * mm, v(-7.84, -56.78) * mm, v(-8.78, -56.78) * mm]});
            skFitSpline(sketch, "E858", {"points": [v(-8.78, -56.78) * mm, v(-10, -56.78) * mm, v(-10.82, -56.44) * mm, v(-11.23, -55.76) * mm]});
            skFitSpline(sketch, "E859", {"points": [v(-11.23, -55.76) * mm, v(-11.65, -55.08) * mm, v(-11.85, -54.27) * mm, v(-11.85, -53.35) * mm]});
            skFitSpline(sketch, "E860", {"points": [v(-11.85, -53.35) * mm, v(-11.85, -51.05) * mm, v(-10.83, -49.9) * mm, v(-8.78, -49.9) * mm]});
            skSolve(sketch);
        }
        {
            var Q0;
            Q0 = qSketchRegion(id + "F5", true);
            extrude(context, id + "F6", {"entities" : qUnion([Q0]), "operationType" : NewBodyOperationType.ADD, "depth" : 1 * mm, "offsetDistance" : 25 * mm});
        }
    });
